# Revit family: HUS-AP-011_EU+APAC_EN
name_source: partatom
category: Casework
units: mm (PartAtom-declared; Revit-internal decimal feet)

## family parameters
Always vertical = Yes
Cut with Voids When Loaded = No
OmniClass Number = 23.40.35.00
OmniClass Title = Casework
Room Calculation Point = Yes
Shared = No
Work Plane-Based = No

## types (640) — shared parameters
Assembly Code = E2010200
Catalogue = https://hushoffice.com
Configurator = https://mikomax.actumwork.pl
Construction Type = Defined construction
Depth = 900 mm  [stored 2.95276 ft]
Equipment - Fixed table = Fixed table : with seat
Equipment - Fixed table with TV mount = Fixed table : with seat + TV holder
Equipment = Movable table = Movable table
Fabric color - seat = ATHLON PLUS Beige
Finish = Defined materials
Handle and hinges = Anodowane aluminium JAL
Height = 2300 mm  [stored 7.54593 ft]
IfcExportAs = IfcFurniture
Manufacturer = Mikomax Smart Office
Region = EU/APAC
Type Image = <None>
URL = https://hushoffice.com
Width = 1245 mm  [stored 4.08465 ft]
zero-valued in all types: Default Elevation

## per-type parameters (varying)
| type | Back glass colour | Counter color | Fabric | Main body | Plug type |
| ABB/001/PRZ/PRZ/EUR/ABB/GPT | Transparent Glass PRZ | White ABB | ATHLON PLUS Blue | White ABB | GPT - Plug type G |
| AGC/001/PRZ/PRZ/EUR/ABB/GPT | Transparent Glass PRZ | White ABB | ATHLON PLUS Blue | Cosmos Grey AGC | GPT - Plug type G |
| ABB/002/PRZ/PRZ/EUR/ABB/GPT | Transparent Glass PRZ | White ABB | ATHLON PLUS Dark grey | White ABB | GPT - Plug type G |
| AGC/002/PRZ/PRZ/EUR/ABB/GPT | Transparent Glass PRZ | White ABB | ATHLON PLUS Dark grey | Cosmos Grey AGC | GPT - Plug type G |
| ABB/003/PRZ/PRZ/EUR/ABB/GPT | Transparent Glass PRZ | White ABB | ATHLON PLUS Light grey | White ABB | GPT - Plug type G |
| AGC/003/PRZ/PRZ/EUR/ABB/GPT | Transparent Glass PRZ | White ABB | ATHLON PLUS Light grey | Cosmos Grey AGC | GPT - Plug type G |
| ABB/004/PRZ/PRZ/EUR/ABB/GPT | Transparent Glass PRZ | White ABB | ATHLON PLUS Light green | White ABB | GPT - Plug type G |
| AGC/004/PRZ/PRZ/EUR/ABB/GPT | Transparent Glass PRZ | White ABB | ATHLON PLUS Light green | Cosmos Grey AGC | GPT - Plug type G |
| ABB/005/PRZ/PRZ/EUR/ABB/GPT | Transparent Glass PRZ | White ABB | ATHLON PLUS Yellow | White ABB | GPT - Plug type G |
| AGC/005/PRZ/PRZ/EUR/ABB/GPT | Transparent Glass PRZ | White ABB | ATHLON PLUS Yellow | Cosmos Grey AGC | GPT - Plug type G |
| ABB/006/PRZ/PRZ/EUR/ABB/GPT | Transparent Glass PRZ | White ABB | ATHLON PLUS Orange | White ABB | GPT - Plug type G |
| AGC/006/PRZ/PRZ/EUR/ABB/GPT | Transparent Glass PRZ | White ABB | ATHLON PLUS Orange | Cosmos Grey AGC | GPT - Plug type G |
| ABB/007/PRZ/PRZ/EUR/ABB/GPT | Transparent Glass PRZ | White ABB | ATHLON PLUS Beige | White ABB | GPT - Plug type G |
| AGC/007/PRZ/PRZ/EUR/ABB/GPT | Transparent Glass PRZ | White ABB | ATHLON PLUS Beige | Cosmos Grey AGC | GPT - Plug type G |
| ABB/008/PRZ/PRZ/EUR/ABB/GPT | Transparent Glass PRZ | White ABB | ATHLON PLUS Red | White ABB | GPT - Plug type G |
| AGC/008/PRZ/PRZ/EUR/ABB/GPT | Transparent Glass PRZ | White ABB | ATHLON PLUS Red | Cosmos Grey AGC | GPT - Plug type G |
| ABB/001/PRZ/MGA/EUR/ABB/GPT | Milk Glass MGA | White ABB | ATHLON PLUS Blue | White ABB | GPT - Plug type G |
| AGC/001/PRZ/MGA/EUR/ABB/GPT | Milk Glass MGA | White ABB | ATHLON PLUS Blue | Cosmos Grey AGC | GPT - Plug type G |
| ABB/002/PRZ/MGA/EUR/ABB/GPT | Milk Glass MGA | White ABB | ATHLON PLUS Dark grey | White ABB | GPT - Plug type G |
| AGC/002/PRZ/MGA/EUR/ABB/GPT | Milk Glass MGA | White ABB | ATHLON PLUS Dark grey | Cosmos Grey AGC | GPT - Plug type G |
| ABB/003/PRZ/MGA/EUR/ABB/GPT | Milk Glass MGA | White ABB | ATHLON PLUS Light grey | White ABB | GPT - Plug type G |
| AGC/003/PRZ/MGA/EUR/ABB/GPT | Milk Glass MGA | White ABB | ATHLON PLUS Light grey | Cosmos Grey AGC | GPT - Plug type G |
| ABB/004/PRZ/MGA/EUR/ABB/GPT | Milk Glass MGA | White ABB | ATHLON PLUS Light green | White ABB | GPT - Plug type G |
| AGC/004/PRZ/MGA/EUR/ABB/GPT | Milk Glass MGA | White ABB | ATHLON PLUS Light green | Cosmos Grey AGC | GPT - Plug type G |
| ABB/005/PRZ/MGA/EUR/ABB/GPT | Milk Glass MGA | White ABB | ATHLON PLUS Yellow | White ABB | GPT - Plug type G |
| AGC/005/PRZ/MGA/EUR/ABB/GPT | Milk Glass MGA | White ABB | ATHLON PLUS Yellow | Cosmos Grey AGC | GPT - Plug type G |
| ABB/006/PRZ/MGA/EUR/ABB/GPT | Milk Glass MGA | White ABB | ATHLON PLUS Orange | White ABB | GPT - Plug type G |
| AGC/006/PRZ/MGA/EUR/ABB/GPT | Milk Glass MGA | White ABB | ATHLON PLUS Orange | Cosmos Grey AGC | GPT - Plug type G |
| ABB/007/PRZ/MGA/EUR/ABB/GPT | Milk Glass MGA | White ABB | ATHLON PLUS Beige | White ABB | GPT - Plug type G |
| AGC/007/PRZ/MGA/EUR/ABB/GPT | Milk Glass MGA | White ABB | ATHLON PLUS Beige | Cosmos Grey AGC | GPT - Plug type G |
| ABB/008/PRZ/MGA/EUR/ABB/GPT | Milk Glass MGA | White ABB | ATHLON PLUS Red | White ABB | GPT - Plug type G |
| AGC/008/PRZ/MGA/EUR/ABB/GPT | Milk Glass MGA | White ABB | ATHLON PLUS Red | Cosmos Grey AGC | GPT - Plug type G |
| ABB/001/PRZ/PRZ/APA/ABB/GPT | Transparent Glass PRZ | White ABB | ATHLON PLUS Blue | White ABB | GPT - Plug type G |
| AGC/001/PRZ/PRZ/APA/ABB/GPT | Transparent Glass PRZ | White ABB | ATHLON PLUS Blue | Cosmos Grey AGC | GPT - Plug type G |
| ABB/002/PRZ/PRZ/APA/ABB/GPT | Transparent Glass PRZ | White ABB | ATHLON PLUS Dark grey | White ABB | GPT - Plug type G |
| AGC/002/PRZ/PRZ/APA/ABB/GPT | Transparent Glass PRZ | White ABB | ATHLON PLUS Dark grey | Cosmos Grey AGC | GPT - Plug type G |
| ABB/003/PRZ/PRZ/APA/ABB/GPT | Transparent Glass PRZ | White ABB | ATHLON PLUS Light grey | White ABB | GPT - Plug type G |
| AGC/003/PRZ/PRZ/APA/ABB/GPT | Transparent Glass PRZ | White ABB | ATHLON PLUS Light grey | Cosmos Grey AGC | GPT - Plug type G |
| ABB/004/PRZ/PRZ/APA/ABB/GPT | Transparent Glass PRZ | White ABB | ATHLON PLUS Light green | White ABB | GPT - Plug type G |
| AGC/004/PRZ/PRZ/APA/ABB/GPT | Transparent Glass PRZ | White ABB | ATHLON PLUS Light green | Cosmos Grey AGC | GPT - Plug type G |
| ABB/005/PRZ/PRZ/APA/ABB/GPT | Transparent Glass PRZ | White ABB | ATHLON PLUS Yellow | White ABB | GPT - Plug type G |
| AGC/005/PRZ/PRZ/APA/ABB/GPT | Transparent Glass PRZ | White ABB | ATHLON PLUS Yellow | Cosmos Grey AGC | GPT - Plug type G |
| ABB/006/PRZ/PRZ/APA/ABB/GPT | Transparent Glass PRZ | White ABB | ATHLON PLUS Orange | White ABB | GPT - Plug type G |
| AGC/006/PRZ/PRZ/APA/ABB/GPT | Transparent Glass PRZ | White ABB | ATHLON PLUS Orange | Cosmos Grey AGC | GPT - Plug type G |
| ABB/007/PRZ/PRZ/APA/ABB/GPT | Transparent Glass PRZ | White ABB | ATHLON PLUS Beige | White ABB | GPT - Plug type G |
| AGC/007/PRZ/PRZ/APA/ABB/GPT | Transparent Glass PRZ | White ABB | ATHLON PLUS Beige | Cosmos Grey AGC | GPT - Plug type G |
| ABB/008/PRZ/PRZ/APA/ABB/GPT | Transparent Glass PRZ | White ABB | ATHLON PLUS Red | White ABB | GPT - Plug type G |
| AGC/008/PRZ/PRZ/APA/ABB/GPT | Transparent Glass PRZ | White ABB | ATHLON PLUS Red | Cosmos Grey AGC | GPT - Plug type G |
| ABB/001/PRZ/MGA/APA/ABB/GPT | Milk Glass MGA | White ABB | ATHLON PLUS Blue | White ABB | GPT - Plug type G |
| AGC/001/PRZ/MGA/APA/ABB/GPT | Milk Glass MGA | White ABB | ATHLON PLUS Blue | Cosmos Grey AGC | GPT - Plug type G |
| ABB/002/PRZ/MGA/APA/ABB/GPT | Milk Glass MGA | White ABB | ATHLON PLUS Dark grey | White ABB | GPT - Plug type G |
| AGC/002/PRZ/MGA/APA/ABB/GPT | Milk Glass MGA | White ABB | ATHLON PLUS Dark grey | Cosmos Grey AGC | GPT - Plug type G |
| ABB/003/PRZ/MGA/APA/ABB/GPT | Milk Glass MGA | White ABB | ATHLON PLUS Light grey | White ABB | GPT - Plug type G |
| AGC/003/PRZ/MGA/APA/ABB/GPT | Milk Glass MGA | White ABB | ATHLON PLUS Light grey | Cosmos Grey AGC | GPT - Plug type G |
| ABB/004/PRZ/MGA/APA/ABB/GPT | Milk Glass MGA | White ABB | ATHLON PLUS Light green | White ABB | GPT - Plug type G |
| AGC/004/PRZ/MGA/APA/ABB/GPT | Milk Glass MGA | White ABB | ATHLON PLUS Light green | Cosmos Grey AGC | GPT - Plug type G |
| ABB/005/PRZ/MGA/APA/ABB/GPT | Milk Glass MGA | White ABB | ATHLON PLUS Yellow | White ABB | GPT - Plug type G |
| AGC/005/PRZ/MGA/APA/ABB/GPT | Milk Glass MGA | White ABB | ATHLON PLUS Yellow | Cosmos Grey AGC | GPT - Plug type G |
| ABB/006/PRZ/MGA/APA/ABB/GPT | Milk Glass MGA | White ABB | ATHLON PLUS Orange | White ABB | GPT - Plug type G |
| AGC/006/PRZ/MGA/APA/ABB/GPT | Milk Glass MGA | White ABB | ATHLON PLUS Orange | Cosmos Grey AGC | GPT - Plug type G |
| ABB/007/PRZ/MGA/APA/ABB/GPT | Milk Glass MGA | White ABB | ATHLON PLUS Beige | White ABB | GPT - Plug type G |
| AGC/007/PRZ/MGA/APA/ABB/GPT | Milk Glass MGA | White ABB | ATHLON PLUS Beige | Cosmos Grey AGC | GPT - Plug type G |
| ABB/008/PRZ/MGA/APA/ABB/GPT | Milk Glass MGA | White ABB | ATHLON PLUS Red | White ABB | GPT - Plug type G |
| AGC/008/PRZ/MGA/APA/ABB/GPT | Milk Glass MGA | White ABB | ATHLON PLUS Red | Cosmos Grey AGC | GPT - Plug type G |
| ABB/001/PRZ/PRZ/EUR/AGA/GPT | Transparent Glass PRZ | Velvet Black AGA | ATHLON PLUS Blue | White ABB | GPT - Plug type G |
| AGC/001/PRZ/PRZ/EUR/AGA/GPT | Transparent Glass PRZ | Velvet Black AGA | ATHLON PLUS Blue | Cosmos Grey AGC | GPT - Plug type G |
| ABB/002/PRZ/PRZ/EUR/AGA/GPT | Transparent Glass PRZ | Velvet Black AGA | ATHLON PLUS Dark grey | White ABB | GPT - Plug type G |
| AGC/002/PRZ/PRZ/EUR/AGA/GPT | Transparent Glass PRZ | Velvet Black AGA | ATHLON PLUS Dark grey | Cosmos Grey AGC | GPT - Plug type G |
| ABB/003/PRZ/PRZ/EUR/AGA/GPT | Transparent Glass PRZ | Velvet Black AGA | ATHLON PLUS Light grey | White ABB | GPT - Plug type G |
| AGC/003/PRZ/PRZ/EUR/AGA/GPT | Transparent Glass PRZ | Velvet Black AGA | ATHLON PLUS Light grey | Cosmos Grey AGC | GPT - Plug type G |
| ABB/004/PRZ/PRZ/EUR/AGA/GPT | Transparent Glass PRZ | Velvet Black AGA | ATHLON PLUS Light green | White ABB | GPT - Plug type G |
| AGC/004/PRZ/PRZ/EUR/AGA/GPT | Transparent Glass PRZ | Velvet Black AGA | ATHLON PLUS Light green | Cosmos Grey AGC | GPT - Plug type G |
| ABB/005/PRZ/PRZ/EUR/AGA/GPT | Transparent Glass PRZ | Velvet Black AGA | ATHLON PLUS Yellow | White ABB | GPT - Plug type G |
| AGC/005/PRZ/PRZ/EUR/AGA/GPT | Transparent Glass PRZ | Velvet Black AGA | ATHLON PLUS Yellow | Cosmos Grey AGC | GPT - Plug type G |
| ABB/006/PRZ/PRZ/EUR/AGA/GPT | Transparent Glass PRZ | Velvet Black AGA | ATHLON PLUS Orange | White ABB | GPT - Plug type G |
| AGC/006/PRZ/PRZ/EUR/AGA/GPT | Transparent Glass PRZ | Velvet Black AGA | ATHLON PLUS Orange | Cosmos Grey AGC | GPT - Plug type G |
| ABB/007/PRZ/PRZ/EUR/AGA/GPT | Transparent Glass PRZ | Velvet Black AGA | ATHLON PLUS Beige | White ABB | GPT - Plug type G |
| AGC/007/PRZ/PRZ/EUR/AGA/GPT | Transparent Glass PRZ | Velvet Black AGA | ATHLON PLUS Beige | Cosmos Grey AGC | GPT - Plug type G |
| ABB/008/PRZ/PRZ/EUR/AGA/GPT | Transparent Glass PRZ | Velvet Black AGA | ATHLON PLUS Red | White ABB | GPT - Plug type G |
| AGC/008/PRZ/PRZ/EUR/AGA/GPT | Transparent Glass PRZ | Velvet Black AGA | ATHLON PLUS Red | Cosmos Grey AGC | GPT - Plug type G |
| ABB/001/PRZ/MGA/EUR/AGA/GPT | Milk Glass MGA | Velvet Black AGA | ATHLON PLUS Blue | White ABB | GPT - Plug type G |
| AGC/001/PRZ/MGA/EUR/AGA/GPT | Milk Glass MGA | Velvet Black AGA | ATHLON PLUS Blue | Cosmos Grey AGC | GPT - Plug type G |
| ABB/002/PRZ/MGA/EUR/AGA/GPT | Milk Glass MGA | Velvet Black AGA | ATHLON PLUS Dark grey | White ABB | GPT - Plug type G |
| AGC/002/PRZ/MGA/EUR/AGA/GPT | Milk Glass MGA | Velvet Black AGA | ATHLON PLUS Dark grey | Cosmos Grey AGC | GPT - Plug type G |
| ABB/003/PRZ/MGA/EUR/AGA/GPT | Milk Glass MGA | Velvet Black AGA | ATHLON PLUS Light grey | White ABB | GPT - Plug type G |
| AGC/003/PRZ/MGA/EUR/AGA/GPT | Milk Glass MGA | Velvet Black AGA | ATHLON PLUS Light grey | Cosmos Grey AGC | GPT - Plug type G |
| ABB/004/PRZ/MGA/EUR/AGA/GPT | Milk Glass MGA | Velvet Black AGA | ATHLON PLUS Light green | White ABB | GPT - Plug type G |
| AGC/004/PRZ/MGA/EUR/AGA/GPT | Milk Glass MGA | Velvet Black AGA | ATHLON PLUS Light green | Cosmos Grey AGC | GPT - Plug type G |
| ABB/005/PRZ/MGA/EUR/AGA/GPT | Milk Glass MGA | Velvet Black AGA | ATHLON PLUS Yellow | White ABB | GPT - Plug type G |
| AGC/005/PRZ/MGA/EUR/AGA/GPT | Milk Glass MGA | Velvet Black AGA | ATHLON PLUS Yellow | Cosmos Grey AGC | GPT - Plug type G |
| ABB/006/PRZ/MGA/EUR/AGA/GPT | Milk Glass MGA | Velvet Black AGA | ATHLON PLUS Orange | White ABB | GPT - Plug type G |
| AGC/006/PRZ/MGA/EUR/AGA/GPT | Milk Glass MGA | Velvet Black AGA | ATHLON PLUS Orange | Cosmos Grey AGC | GPT - Plug type G |
| ABB/007/PRZ/MGA/EUR/AGA/GPT | Milk Glass MGA | Velvet Black AGA | ATHLON PLUS Beige | White ABB | GPT - Plug type G |
| AGC/007/PRZ/MGA/EUR/AGA/GPT | Milk Glass MGA | Velvet Black AGA | ATHLON PLUS Beige | Cosmos Grey AGC | GPT - Plug type G |
| ABB/008/PRZ/MGA/EUR/AGA/GPT | Milk Glass MGA | Velvet Black AGA | ATHLON PLUS Red | White ABB | GPT - Plug type G |
| AGC/008/PRZ/MGA/EUR/AGA/GPT | Milk Glass MGA | Velvet Black AGA | ATHLON PLUS Red | Cosmos Grey AGC | GPT - Plug type G |
| ABB/001/PRZ/PRZ/APA/AGA/GPT | Transparent Glass PRZ | Velvet Black AGA | ATHLON PLUS Blue | White ABB | GPT - Plug type G |
| AGC/001/PRZ/PRZ/APA/AGA/GPT | Transparent Glass PRZ | Velvet Black AGA | ATHLON PLUS Blue | Cosmos Grey AGC | GPT - Plug type G |
| ABB/002/PRZ/PRZ/APA/AGA/GPT | Transparent Glass PRZ | Velvet Black AGA | ATHLON PLUS Dark grey | White ABB | GPT - Plug type G |
| AGC/002/PRZ/PRZ/APA/AGA/GPT | Transparent Glass PRZ | Velvet Black AGA | ATHLON PLUS Dark grey | Cosmos Grey AGC | GPT - Plug type G |
| ABB/003/PRZ/PRZ/APA/AGA/GPT | Transparent Glass PRZ | Velvet Black AGA | ATHLON PLUS Light grey | White ABB | GPT - Plug type G |
| AGC/003/PRZ/PRZ/APA/AGA/GPT | Transparent Glass PRZ | Velvet Black AGA | ATHLON PLUS Light grey | Cosmos Grey AGC | GPT - Plug type G |
| ABB/004/PRZ/PRZ/APA/AGA/GPT | Transparent Glass PRZ | Velvet Black AGA | ATHLON PLUS Light green | White ABB | GPT - Plug type G |
| AGC/004/PRZ/PRZ/APA/AGA/GPT | Transparent Glass PRZ | Velvet Black AGA | ATHLON PLUS Light green | Cosmos Grey AGC | GPT - Plug type G |
| ABB/005/PRZ/PRZ/APA/AGA/GPT | Transparent Glass PRZ | Velvet Black AGA | ATHLON PLUS Yellow | White ABB | GPT - Plug type G |
| AGC/005/PRZ/PRZ/APA/AGA/GPT | Transparent Glass PRZ | Velvet Black AGA | ATHLON PLUS Yellow | Cosmos Grey AGC | GPT - Plug type G |
| ABB/006/PRZ/PRZ/APA/AGA/GPT | Transparent Glass PRZ | Velvet Black AGA | ATHLON PLUS Orange | White ABB | GPT - Plug type G |
| AGC/006/PRZ/PRZ/APA/AGA/GPT | Transparent Glass PRZ | Velvet Black AGA | ATHLON PLUS Orange | Cosmos Grey AGC | GPT - Plug type G |
| ABB/007/PRZ/PRZ/APA/AGA/GPT | Transparent Glass PRZ | Velvet Black AGA | ATHLON PLUS Beige | White ABB | GPT - Plug type G |
| AGC/007/PRZ/PRZ/APA/AGA/GPT | Transparent Glass PRZ | Velvet Black AGA | ATHLON PLUS Beige | Cosmos Grey AGC | GPT - Plug type G |
| ABB/008/PRZ/PRZ/APA/AGA/GPT | Transparent Glass PRZ | Velvet Black AGA | ATHLON PLUS Red | White ABB | GPT - Plug type G |
| AGC/008/PRZ/PRZ/APA/AGA/GPT | Transparent Glass PRZ | Velvet Black AGA | ATHLON PLUS Red | Cosmos Grey AGC | GPT - Plug type G |
| ABB/001/PRZ/MGA/APA/AGA/GPT | Milk Glass MGA | Velvet Black AGA | ATHLON PLUS Blue | White ABB | GPT - Plug type G |
| AGC/001/PRZ/MGA/APA/AGA/GPT | Milk Glass MGA | Velvet Black AGA | ATHLON PLUS Blue | Cosmos Grey AGC | GPT - Plug type G |
| ABB/002/PRZ/MGA/APA/AGA/GPT | Milk Glass MGA | Velvet Black AGA | ATHLON PLUS Dark grey | White ABB | GPT - Plug type G |
| AGC/002/PRZ/MGA/APA/AGA/GPT | Milk Glass MGA | Velvet Black AGA | ATHLON PLUS Dark grey | Cosmos Grey AGC | GPT - Plug type G |
| ABB/003/PRZ/MGA/APA/AGA/GPT | Milk Glass MGA | Velvet Black AGA | ATHLON PLUS Light grey | White ABB | GPT - Plug type G |
| AGC/003/PRZ/MGA/APA/AGA/GPT | Milk Glass MGA | Velvet Black AGA | ATHLON PLUS Light grey | Cosmos Grey AGC | GPT - Plug type G |
| ABB/004/PRZ/MGA/APA/AGA/GPT | Milk Glass MGA | Velvet Black AGA | ATHLON PLUS Light green | White ABB | GPT - Plug type G |
| AGC/004/PRZ/MGA/APA/AGA/GPT | Milk Glass MGA | Velvet Black AGA | ATHLON PLUS Light green | Cosmos Grey AGC | GPT - Plug type G |
| ABB/005/PRZ/MGA/APA/AGA/GPT | Milk Glass MGA | Velvet Black AGA | ATHLON PLUS Yellow | White ABB | GPT - Plug type G |
| AGC/005/PRZ/MGA/APA/AGA/GPT | Milk Glass MGA | Velvet Black AGA | ATHLON PLUS Yellow | Cosmos Grey AGC | GPT - Plug type G |
| ABB/006/PRZ/MGA/APA/AGA/GPT | Milk Glass MGA | Velvet Black AGA | ATHLON PLUS Orange | White ABB | GPT - Plug type G |
| AGC/006/PRZ/MGA/APA/AGA/GPT | Milk Glass MGA | Velvet Black AGA | ATHLON PLUS Orange | Cosmos Grey AGC | GPT - Plug type G |
| ABB/007/PRZ/MGA/APA/AGA/GPT | Milk Glass MGA | Velvet Black AGA | ATHLON PLUS Beige | White ABB | GPT - Plug type G |
| AGC/007/PRZ/MGA/APA/AGA/GPT | Milk Glass MGA | Velvet Black AGA | ATHLON PLUS Beige | Cosmos Grey AGC | GPT - Plug type G |
| ABB/008/PRZ/MGA/APA/AGA/GPT | Milk Glass MGA | Velvet Black AGA | ATHLON PLUS Red | White ABB | GPT - Plug type G |
| AGC/008/PRZ/MGA/APA/AGA/GPT | Milk Glass MGA | Velvet Black AGA | ATHLON PLUS Red | Cosmos Grey AGC | GPT - Plug type G |
| ABB/001/PRZ/PRZ/EUR/ABB/FPT | Transparent Glass PRZ | White ABB | ATHLON PLUS Blue | White ABB | FPT - Plug type F |
| AGC/001/PRZ/PRZ/EUR/ABB/FPT | Transparent Glass PRZ | White ABB | ATHLON PLUS Blue | Cosmos Grey AGC | FPT - Plug type F |
| ABB/002/PRZ/PRZ/EUR/ABB/FPT | Transparent Glass PRZ | White ABB | ATHLON PLUS Dark grey | White ABB | FPT - Plug type F |
| AGC/002/PRZ/PRZ/EUR/ABB/FPT | Transparent Glass PRZ | White ABB | ATHLON PLUS Dark grey | Cosmos Grey AGC | FPT - Plug type F |
| ABB/003/PRZ/PRZ/EUR/ABB/FPT | Transparent Glass PRZ | White ABB | ATHLON PLUS Light grey | White ABB | FPT - Plug type F |
| AGC/003/PRZ/PRZ/EUR/ABB/FPT | Transparent Glass PRZ | White ABB | ATHLON PLUS Light grey | Cosmos Grey AGC | FPT - Plug type F |
| ABB/004/PRZ/PRZ/EUR/ABB/FPT | Transparent Glass PRZ | White ABB | ATHLON PLUS Light green | White ABB | FPT - Plug type F |
| AGC/004/PRZ/PRZ/EUR/ABB/FPT | Transparent Glass PRZ | White ABB | ATHLON PLUS Light green | Cosmos Grey AGC | FPT - Plug type F |
| ABB/005/PRZ/PRZ/EUR/ABB/FPT | Transparent Glass PRZ | White ABB | ATHLON PLUS Yellow | White ABB | FPT - Plug type F |
| AGC/005/PRZ/PRZ/EUR/ABB/FPT | Transparent Glass PRZ | White ABB | ATHLON PLUS Yellow | Cosmos Grey AGC | FPT - Plug type F |
| ABB/006/PRZ/PRZ/EUR/ABB/FPT | Transparent Glass PRZ | White ABB | ATHLON PLUS Orange | White ABB | FPT - Plug type F |
| AGC/006/PRZ/PRZ/EUR/ABB/FPT | Transparent Glass PRZ | White ABB | ATHLON PLUS Orange | Cosmos Grey AGC | FPT - Plug type F |
| ABB/007/PRZ/PRZ/EUR/ABB/FPT | Transparent Glass PRZ | White ABB | ATHLON PLUS Beige | White ABB | FPT - Plug type F |
| AGC/007/PRZ/PRZ/EUR/ABB/FPT | Transparent Glass PRZ | White ABB | ATHLON PLUS Beige | Cosmos Grey AGC | FPT - Plug type F |
| ABB/008/PRZ/PRZ/EUR/ABB/FPT | Transparent Glass PRZ | White ABB | ATHLON PLUS Red | White ABB | FPT - Plug type F |
| AGC/008/PRZ/PRZ/EUR/ABB/FPT | Transparent Glass PRZ | White ABB | ATHLON PLUS Red | Cosmos Grey AGC | FPT - Plug type F |
| ABB/001/PRZ/MGA/EUR/ABB/FPT | Milk Glass MGA | White ABB | ATHLON PLUS Blue | White ABB | FPT - Plug type F |
| AGC/001/PRZ/MGA/EUR/ABB/FPT | Milk Glass MGA | White ABB | ATHLON PLUS Blue | Cosmos Grey AGC | FPT - Plug type F |
| ABB/002/PRZ/MGA/EUR/ABB/FPT | Milk Glass MGA | White ABB | ATHLON PLUS Dark grey | White ABB | FPT - Plug type F |
| AGC/002/PRZ/MGA/EUR/ABB/FPT | Milk Glass MGA | White ABB | ATHLON PLUS Dark grey | Cosmos Grey AGC | FPT - Plug type F |
| ABB/003/PRZ/MGA/EUR/ABB/FPT | Milk Glass MGA | White ABB | ATHLON PLUS Light grey | White ABB | FPT - Plug type F |
| AGC/003/PRZ/MGA/EUR/ABB/FPT | Milk Glass MGA | White ABB | ATHLON PLUS Light grey | Cosmos Grey AGC | FPT - Plug type F |
| ABB/004/PRZ/MGA/EUR/ABB/FPT | Milk Glass MGA | White ABB | ATHLON PLUS Light green | White ABB | FPT - Plug type F |
| AGC/004/PRZ/MGA/EUR/ABB/FPT | Milk Glass MGA | White ABB | ATHLON PLUS Light green | Cosmos Grey AGC | FPT - Plug type F |
| ABB/005/PRZ/MGA/EUR/ABB/FPT | Milk Glass MGA | White ABB | ATHLON PLUS Yellow | White ABB | FPT - Plug type F |
| AGC/005/PRZ/MGA/EUR/ABB/FPT | Milk Glass MGA | White ABB | ATHLON PLUS Yellow | Cosmos Grey AGC | FPT - Plug type F |
| ABB/006/PRZ/MGA/EUR/ABB/FPT | Milk Glass MGA | White ABB | ATHLON PLUS Orange | White ABB | FPT - Plug type F |
| AGC/006/PRZ/MGA/EUR/ABB/FPT | Milk Glass MGA | White ABB | ATHLON PLUS Orange | Cosmos Grey AGC | FPT - Plug type F |
| ABB/007/PRZ/MGA/EUR/ABB/FPT | Milk Glass MGA | White ABB | ATHLON PLUS Beige | White ABB | FPT - Plug type F |
| AGC/007/PRZ/MGA/EUR/ABB/FPT | Milk Glass MGA | White ABB | ATHLON PLUS Beige | Cosmos Grey AGC | FPT - Plug type F |
| ABB/008/PRZ/MGA/EUR/ABB/FPT | Milk Glass MGA | White ABB | ATHLON PLUS Red | White ABB | FPT - Plug type F |
| AGC/008/PRZ/MGA/EUR/ABB/FPT | Milk Glass MGA | White ABB | ATHLON PLUS Red | Cosmos Grey AGC | FPT - Plug type F |
| ABB/001/PRZ/PRZ/APA/ABB/FPT | Transparent Glass PRZ | White ABB | ATHLON PLUS Blue | White ABB | FPT - Plug type F |
| AGC/001/PRZ/PRZ/APA/ABB/FPT | Transparent Glass PRZ | White ABB | ATHLON PLUS Blue | Cosmos Grey AGC | FPT - Plug type F |
| ABB/002/PRZ/PRZ/APA/ABB/FPT | Transparent Glass PRZ | White ABB | ATHLON PLUS Dark grey | White ABB | FPT - Plug type F |
| AGC/002/PRZ/PRZ/APA/ABB/FPT | Transparent Glass PRZ | White ABB | ATHLON PLUS Dark grey | Cosmos Grey AGC | FPT - Plug type F |
| ABB/003/PRZ/PRZ/APA/ABB/FPT | Transparent Glass PRZ | White ABB | ATHLON PLUS Light grey | White ABB | FPT - Plug type F |
| AGC/003/PRZ/PRZ/APA/ABB/FPT | Transparent Glass PRZ | White ABB | ATHLON PLUS Light grey | Cosmos Grey AGC | FPT - Plug type F |
| ABB/004/PRZ/PRZ/APA/ABB/FPT | Transparent Glass PRZ | White ABB | ATHLON PLUS Light green | White ABB | FPT - Plug type F |
| AGC/004/PRZ/PRZ/APA/ABB/FPT | Transparent Glass PRZ | White ABB | ATHLON PLUS Light green | Cosmos Grey AGC | FPT - Plug type F |
| ABB/005/PRZ/PRZ/APA/ABB/FPT | Transparent Glass PRZ | White ABB | ATHLON PLUS Yellow | White ABB | FPT - Plug type F |
| AGC/005/PRZ/PRZ/APA/ABB/FPT | Transparent Glass PRZ | White ABB | ATHLON PLUS Yellow | Cosmos Grey AGC | FPT - Plug type F |
| ABB/006/PRZ/PRZ/APA/ABB/FPT | Transparent Glass PRZ | White ABB | ATHLON PLUS Orange | White ABB | FPT - Plug type F |
| AGC/006/PRZ/PRZ/APA/ABB/FPT | Transparent Glass PRZ | White ABB | ATHLON PLUS Orange | Cosmos Grey AGC | FPT - Plug type F |
| ABB/007/PRZ/PRZ/APA/ABB/FPT | Transparent Glass PRZ | White ABB | ATHLON PLUS Beige | White ABB | FPT - Plug type F |
| AGC/007/PRZ/PRZ/APA/ABB/FPT | Transparent Glass PRZ | White ABB | ATHLON PLUS Beige | Cosmos Grey AGC | FPT - Plug type F |
| ABB/008/PRZ/PRZ/APA/ABB/FPT | Transparent Glass PRZ | White ABB | ATHLON PLUS Red | White ABB | FPT - Plug type F |
| AGC/008/PRZ/PRZ/APA/ABB/FPT | Transparent Glass PRZ | White ABB | ATHLON PLUS Red | Cosmos Grey AGC | FPT - Plug type F |
| ABB/001/PRZ/MGA/APA/ABB/FPT | Milk Glass MGA | White ABB | ATHLON PLUS Blue | White ABB | FPT - Plug type F |
| AGC/001/PRZ/MGA/APA/ABB/FPT | Milk Glass MGA | White ABB | ATHLON PLUS Blue | Cosmos Grey AGC | FPT - Plug type F |
| ABB/002/PRZ/MGA/APA/ABB/FPT | Milk Glass MGA | White ABB | ATHLON PLUS Dark grey | White ABB | FPT - Plug type F |
| AGC/002/PRZ/MGA/APA/ABB/FPT | Milk Glass MGA | White ABB | ATHLON PLUS Dark grey | Cosmos Grey AGC | FPT - Plug type F |
| ABB/003/PRZ/MGA/APA/ABB/FPT | Milk Glass MGA | White ABB | ATHLON PLUS Light grey | White ABB | FPT - Plug type F |
| AGC/003/PRZ/MGA/APA/ABB/FPT | Milk Glass MGA | White ABB | ATHLON PLUS Light grey | Cosmos Grey AGC | FPT - Plug type F |
| ABB/004/PRZ/MGA/APA/ABB/FPT | Milk Glass MGA | White ABB | ATHLON PLUS Light green | White ABB | FPT - Plug type F |
| AGC/004/PRZ/MGA/APA/ABB/FPT | Milk Glass MGA | White ABB | ATHLON PLUS Light green | Cosmos Grey AGC | FPT - Plug type F |
| ABB/005/PRZ/MGA/APA/ABB/FPT | Milk Glass MGA | White ABB | ATHLON PLUS Yellow | White ABB | FPT - Plug type F |
| AGC/005/PRZ/MGA/APA/ABB/FPT | Milk Glass MGA | White ABB | ATHLON PLUS Yellow | Cosmos Grey AGC | FPT - Plug type F |
| ABB/006/PRZ/MGA/APA/ABB/FPT | Milk Glass MGA | White ABB | ATHLON PLUS Orange | White ABB | FPT - Plug type F |
| AGC/006/PRZ/MGA/APA/ABB/FPT | Milk Glass MGA | White ABB | ATHLON PLUS Orange | Cosmos Grey AGC | FPT - Plug type F |
| ABB/007/PRZ/MGA/APA/ABB/FPT | Milk Glass MGA | White ABB | ATHLON PLUS Beige | White ABB | FPT - Plug type F |
| AGC/007/PRZ/MGA/APA/ABB/FPT | Milk Glass MGA | White ABB | ATHLON PLUS Beige | Cosmos Grey AGC | FPT - Plug type F |
| ABB/008/PRZ/MGA/APA/ABB/FPT | Milk Glass MGA | White ABB | ATHLON PLUS Red | White ABB | FPT - Plug type F |
| AGC/008/PRZ/MGA/APA/ABB/FPT | Milk Glass MGA | White ABB | ATHLON PLUS Red | Cosmos Grey AGC | FPT - Plug type F |
| ABB/001/PRZ/PRZ/EUR/AGA/FPT | Transparent Glass PRZ | Velvet Black AGA | ATHLON PLUS Blue | White ABB | FPT - Plug type F |
| AGC/001/PRZ/PRZ/EUR/AGA/FPT | Transparent Glass PRZ | Velvet Black AGA | ATHLON PLUS Blue | Cosmos Grey AGC | FPT - Plug type F |
| ABB/002/PRZ/PRZ/EUR/AGA/FPT | Transparent Glass PRZ | Velvet Black AGA | ATHLON PLUS Dark grey | White ABB | FPT - Plug type F |
| AGC/002/PRZ/PRZ/EUR/AGA/FPT | Transparent Glass PRZ | Velvet Black AGA | ATHLON PLUS Dark grey | Cosmos Grey AGC | FPT - Plug type F |
| ABB/003/PRZ/PRZ/EUR/AGA/FPT | Transparent Glass PRZ | Velvet Black AGA | ATHLON PLUS Light grey | White ABB | FPT - Plug type F |
| AGC/003/PRZ/PRZ/EUR/AGA/FPT | Transparent Glass PRZ | Velvet Black AGA | ATHLON PLUS Light grey | Cosmos Grey AGC | FPT - Plug type F |
| ABB/004/PRZ/PRZ/EUR/AGA/FPT | Transparent Glass PRZ | Velvet Black AGA | ATHLON PLUS Light green | White ABB | FPT - Plug type F |
| AGC/004/PRZ/PRZ/EUR/AGA/FPT | Transparent Glass PRZ | Velvet Black AGA | ATHLON PLUS Light green | Cosmos Grey AGC | FPT - Plug type F |
| ABB/005/PRZ/PRZ/EUR/AGA/FPT | Transparent Glass PRZ | Velvet Black AGA | ATHLON PLUS Yellow | White ABB | FPT - Plug type F |
| AGC/005/PRZ/PRZ/EUR/AGA/FPT | Transparent Glass PRZ | Velvet Black AGA | ATHLON PLUS Yellow | Cosmos Grey AGC | FPT - Plug type F |
| ABB/006/PRZ/PRZ/EUR/AGA/FPT | Transparent Glass PRZ | Velvet Black AGA | ATHLON PLUS Orange | White ABB | FPT - Plug type F |
| AGC/006/PRZ/PRZ/EUR/AGA/FPT | Transparent Glass PRZ | Velvet Black AGA | ATHLON PLUS Orange | Cosmos Grey AGC | FPT - Plug type F |
| ABB/007/PRZ/PRZ/EUR/AGA/FPT | Transparent Glass PRZ | Velvet Black AGA | ATHLON PLUS Beige | White ABB | FPT - Plug type F |
| AGC/007/PRZ/PRZ/EUR/AGA/FPT | Transparent Glass PRZ | Velvet Black AGA | ATHLON PLUS Beige | Cosmos Grey AGC | FPT - Plug type F |
| ABB/008/PRZ/PRZ/EUR/AGA/FPT | Transparent Glass PRZ | Velvet Black AGA | ATHLON PLUS Red | White ABB | FPT - Plug type F |
| AGC/008/PRZ/PRZ/EUR/AGA/FPT | Transparent Glass PRZ | Velvet Black AGA | ATHLON PLUS Red | Cosmos Grey AGC | FPT - Plug type F |
| ABB/001/PRZ/MGA/EUR/AGA/FPT | Milk Glass MGA | Velvet Black AGA | ATHLON PLUS Blue | White ABB | FPT - Plug type F |
| AGC/001/PRZ/MGA/EUR/AGA/FPT | Milk Glass MGA | Velvet Black AGA | ATHLON PLUS Blue | Cosmos Grey AGC | FPT - Plug type F |
| ABB/002/PRZ/MGA/EUR/AGA/FPT | Milk Glass MGA | Velvet Black AGA | ATHLON PLUS Dark grey | White ABB | FPT - Plug type F |
| AGC/002/PRZ/MGA/EUR/AGA/FPT | Milk Glass MGA | Velvet Black AGA | ATHLON PLUS Dark grey | Cosmos Grey AGC | FPT - Plug type F |
| ABB/003/PRZ/MGA/EUR/AGA/FPT | Milk Glass MGA | Velvet Black AGA | ATHLON PLUS Light grey | White ABB | FPT - Plug type F |
| AGC/003/PRZ/MGA/EUR/AGA/FPT | Milk Glass MGA | Velvet Black AGA | ATHLON PLUS Light grey | Cosmos Grey AGC | FPT - Plug type F |
| ABB/004/PRZ/MGA/EUR/AGA/FPT | Milk Glass MGA | Velvet Black AGA | ATHLON PLUS Light green | White ABB | FPT - Plug type F |
| AGC/004/PRZ/MGA/EUR/AGA/FPT | Milk Glass MGA | Velvet Black AGA | ATHLON PLUS Light green | Cosmos Grey AGC | FPT - Plug type F |
| ABB/005/PRZ/MGA/EUR/AGA/FPT | Milk Glass MGA | Velvet Black AGA | ATHLON PLUS Yellow | White ABB | FPT - Plug type F |
| AGC/005/PRZ/MGA/EUR/AGA/FPT | Milk Glass MGA | Velvet Black AGA | ATHLON PLUS Yellow | Cosmos Grey AGC | FPT - Plug type F |
| ABB/006/PRZ/MGA/EUR/AGA/FPT | Milk Glass MGA | Velvet Black AGA | ATHLON PLUS Orange | White ABB | FPT - Plug type F |
| AGC/006/PRZ/MGA/EUR/AGA/FPT | Milk Glass MGA | Velvet Black AGA | ATHLON PLUS Orange | Cosmos Grey AGC | FPT - Plug type F |
| ABB/007/PRZ/MGA/EUR/AGA/FPT | Milk Glass MGA | Velvet Black AGA | ATHLON PLUS Beige | White ABB | FPT - Plug type F |
| AGC/007/PRZ/MGA/EUR/AGA/FPT | Milk Glass MGA | Velvet Black AGA | ATHLON PLUS Beige | Cosmos Grey AGC | FPT - Plug type F |
| ABB/008/PRZ/MGA/EUR/AGA/FPT | Milk Glass MGA | Velvet Black AGA | ATHLON PLUS Red | White ABB | FPT - Plug type F |
| AGC/008/PRZ/MGA/EUR/AGA/FPT | Milk Glass MGA | Velvet Black AGA | ATHLON PLUS Red | Cosmos Grey AGC | FPT - Plug type F |
| ABB/001/PRZ/PRZ/APA/AGA/FPT | Transparent Glass PRZ | Velvet Black AGA | ATHLON PLUS Blue | White ABB | FPT - Plug type F |
| AGC/001/PRZ/PRZ/APA/AGA/FPT | Transparent Glass PRZ | Velvet Black AGA | ATHLON PLUS Blue | Cosmos Grey AGC | FPT - Plug type F |
| ABB/002/PRZ/PRZ/APA/AGA/FPT | Transparent Glass PRZ | Velvet Black AGA | ATHLON PLUS Dark grey | White ABB | FPT - Plug type F |
| AGC/002/PRZ/PRZ/APA/AGA/FPT | Transparent Glass PRZ | Velvet Black AGA | ATHLON PLUS Dark grey | Cosmos Grey AGC | FPT - Plug type F |
| ABB/003/PRZ/PRZ/APA/AGA/FPT | Transparent Glass PRZ | Velvet Black AGA | ATHLON PLUS Light grey | White ABB | FPT - Plug type F |
| AGC/003/PRZ/PRZ/APA/AGA/FPT | Transparent Glass PRZ | Velvet Black AGA | ATHLON PLUS Light grey | Cosmos Grey AGC | FPT - Plug type F |
| ABB/004/PRZ/PRZ/APA/AGA/FPT | Transparent Glass PRZ | Velvet Black AGA | ATHLON PLUS Light green | White ABB | FPT - Plug type F |
| AGC/004/PRZ/PRZ/APA/AGA/FPT | Transparent Glass PRZ | Velvet Black AGA | ATHLON PLUS Light green | Cosmos Grey AGC | FPT - Plug type F |
| ABB/005/PRZ/PRZ/APA/AGA/FPT | Transparent Glass PRZ | Velvet Black AGA | ATHLON PLUS Yellow | White ABB | FPT - Plug type F |
| AGC/005/PRZ/PRZ/APA/AGA/FPT | Transparent Glass PRZ | Velvet Black AGA | ATHLON PLUS Yellow | Cosmos Grey AGC | FPT - Plug type F |
| ABB/006/PRZ/PRZ/APA/AGA/FPT | Transparent Glass PRZ | Velvet Black AGA | ATHLON PLUS Orange | White ABB | FPT - Plug type F |
| AGC/006/PRZ/PRZ/APA/AGA/FPT | Transparent Glass PRZ | Velvet Black AGA | ATHLON PLUS Orange | Cosmos Grey AGC | FPT - Plug type F |
| ABB/007/PRZ/PRZ/APA/AGA/FPT | Transparent Glass PRZ | Velvet Black AGA | ATHLON PLUS Beige | White ABB | FPT - Plug type F |
| AGC/007/PRZ/PRZ/APA/AGA/FPT | Transparent Glass PRZ | Velvet Black AGA | ATHLON PLUS Beige | Cosmos Grey AGC | FPT - Plug type F |
| ABB/008/PRZ/PRZ/APA/AGA/FPT | Transparent Glass PRZ | Velvet Black AGA | ATHLON PLUS Red | White ABB | FPT - Plug type F |
| AGC/008/PRZ/PRZ/APA/AGA/FPT | Transparent Glass PRZ | Velvet Black AGA | ATHLON PLUS Red | Cosmos Grey AGC | FPT - Plug type F |
| ABB/001/PRZ/MGA/APA/AGA/FPT | Milk Glass MGA | Velvet Black AGA | ATHLON PLUS Blue | White ABB | FPT - Plug type F |
| AGC/001/PRZ/MGA/APA/AGA/FPT | Milk Glass MGA | Velvet Black AGA | ATHLON PLUS Blue | Cosmos Grey AGC | FPT - Plug type F |
| ABB/002/PRZ/MGA/APA/AGA/FPT | Milk Glass MGA | Velvet Black AGA | ATHLON PLUS Dark grey | White ABB | FPT - Plug type F |
| AGC/002/PRZ/MGA/APA/AGA/FPT | Milk Glass MGA | Velvet Black AGA | ATHLON PLUS Dark grey | Cosmos Grey AGC | FPT - Plug type F |
| ABB/003/PRZ/MGA/APA/AGA/FPT | Milk Glass MGA | Velvet Black AGA | ATHLON PLUS Light grey | White ABB | FPT - Plug type F |
| AGC/003/PRZ/MGA/APA/AGA/FPT | Milk Glass MGA | Velvet Black AGA | ATHLON PLUS Light grey | Cosmos Grey AGC | FPT - Plug type F |
| ABB/004/PRZ/MGA/APA/AGA/FPT | Milk Glass MGA | Velvet Black AGA | ATHLON PLUS Light green | White ABB | FPT - Plug type F |
| AGC/004/PRZ/MGA/APA/AGA/FPT | Milk Glass MGA | Velvet Black AGA | ATHLON PLUS Light green | Cosmos Grey AGC | FPT - Plug type F |
| ABB/005/PRZ/MGA/APA/AGA/FPT | Milk Glass MGA | Velvet Black AGA | ATHLON PLUS Yellow | White ABB | FPT - Plug type F |
| AGC/005/PRZ/MGA/APA/AGA/FPT | Milk Glass MGA | Velvet Black AGA | ATHLON PLUS Yellow | Cosmos Grey AGC | FPT - Plug type F |
| ABB/006/PRZ/MGA/APA/AGA/FPT | Milk Glass MGA | Velvet Black AGA | ATHLON PLUS Orange | White ABB | FPT - Plug type F |
| AGC/006/PRZ/MGA/APA/AGA/FPT | Milk Glass MGA | Velvet Black AGA | ATHLON PLUS Orange | Cosmos Grey AGC | FPT - Plug type F |
| ABB/007/PRZ/MGA/APA/AGA/FPT | Milk Glass MGA | Velvet Black AGA | ATHLON PLUS Beige | White ABB | FPT - Plug type F |
| AGC/007/PRZ/MGA/APA/AGA/FPT | Milk Glass MGA | Velvet Black AGA | ATHLON PLUS Beige | Cosmos Grey AGC | FPT - Plug type F |
| ABB/008/PRZ/MGA/APA/AGA/FPT | Milk Glass MGA | Velvet Black AGA | ATHLON PLUS Red | White ABB | FPT - Plug type F |
| AGC/008/PRZ/MGA/APA/AGA/FPT | Milk Glass MGA | Velvet Black AGA | ATHLON PLUS Red | Cosmos Grey AGC | FPT - Plug type F |
| ABB/001/PRZ/PRZ/EUR/ABB/EPT | Transparent Glass PRZ | White ABB | ATHLON PLUS Blue | White ABB | EPT - Plug type E |
| AGC/001/PRZ/PRZ/EUR/ABB/EPT | Transparent Glass PRZ | White ABB | ATHLON PLUS Blue | Cosmos Grey AGC | EPT - Plug type E |
| ABB/002/PRZ/PRZ/EUR/ABB/EPT | Transparent Glass PRZ | White ABB | ATHLON PLUS Dark grey | White ABB | EPT - Plug type E |
| AGC/002/PRZ/PRZ/EUR/ABB/EPT | Transparent Glass PRZ | White ABB | ATHLON PLUS Dark grey | Cosmos Grey AGC | EPT - Plug type E |
| ABB/003/PRZ/PRZ/EUR/ABB/EPT | Transparent Glass PRZ | White ABB | ATHLON PLUS Light grey | White ABB | EPT - Plug type E |
| AGC/003/PRZ/PRZ/EUR/ABB/EPT | Transparent Glass PRZ | White ABB | ATHLON PLUS Light grey | Cosmos Grey AGC | EPT - Plug type E |
| ABB/004/PRZ/PRZ/EUR/ABB/EPT | Transparent Glass PRZ | White ABB | ATHLON PLUS Light green | White ABB | EPT - Plug type E |
| AGC/004/PRZ/PRZ/EUR/ABB/EPT | Transparent Glass PRZ | White ABB | ATHLON PLUS Light green | Cosmos Grey AGC | EPT - Plug type E |
| ABB/005/PRZ/PRZ/EUR/ABB/EPT | Transparent Glass PRZ | White ABB | ATHLON PLUS Yellow | White ABB | EPT - Plug type E |
| AGC/005/PRZ/PRZ/EUR/ABB/EPT | Transparent Glass PRZ | White ABB | ATHLON PLUS Yellow | Cosmos Grey AGC | EPT - Plug type E |
| ABB/006/PRZ/PRZ/EUR/ABB/EPT | Transparent Glass PRZ | White ABB | ATHLON PLUS Orange | White ABB | EPT - Plug type E |
| AGC/006/PRZ/PRZ/EUR/ABB/EPT | Transparent Glass PRZ | White ABB | ATHLON PLUS Orange | Cosmos Grey AGC | EPT - Plug type E |
| ABB/007/PRZ/PRZ/EUR/ABB/EPT | Transparent Glass PRZ | White ABB | ATHLON PLUS Beige | White ABB | EPT - Plug type E |
| AGC/007/PRZ/PRZ/EUR/ABB/EPT | Transparent Glass PRZ | White ABB | ATHLON PLUS Beige | Cosmos Grey AGC | EPT - Plug type E |
| ABB/008/PRZ/PRZ/EUR/ABB/EPT | Transparent Glass PRZ | White ABB | ATHLON PLUS Red | White ABB | EPT - Plug type E |
| AGC/008/PRZ/PRZ/EUR/ABB/EPT | Transparent Glass PRZ | White ABB | ATHLON PLUS Red | Cosmos Grey AGC | EPT - Plug type E |
| ABB/001/PRZ/MGA/EUR/ABB/EPT | Milk Glass MGA | White ABB | ATHLON PLUS Blue | White ABB | EPT - Plug type E |
| AGC/001/PRZ/MGA/EUR/ABB/EPT | Milk Glass MGA | White ABB | ATHLON PLUS Blue | Cosmos Grey AGC | EPT - Plug type E |
| ABB/002/PRZ/MGA/EUR/ABB/EPT | Milk Glass MGA | White ABB | ATHLON PLUS Dark grey | White ABB | EPT - Plug type E |
| AGC/002/PRZ/MGA/EUR/ABB/EPT | Milk Glass MGA | White ABB | ATHLON PLUS Dark grey | Cosmos Grey AGC | EPT - Plug type E |
| ABB/003/PRZ/MGA/EUR/ABB/EPT | Milk Glass MGA | White ABB | ATHLON PLUS Light grey | White ABB | EPT - Plug type E |
| AGC/003/PRZ/MGA/EUR/ABB/EPT | Milk Glass MGA | White ABB | ATHLON PLUS Light grey | Cosmos Grey AGC | EPT - Plug type E |
| ABB/004/PRZ/MGA/EUR/ABB/EPT | Milk Glass MGA | White ABB | ATHLON PLUS Light green | White ABB | EPT - Plug type E |
| AGC/004/PRZ/MGA/EUR/ABB/EPT | Milk Glass MGA | White ABB | ATHLON PLUS Light green | Cosmos Grey AGC | EPT - Plug type E |
| ABB/005/PRZ/MGA/EUR/ABB/EPT | Milk Glass MGA | White ABB | ATHLON PLUS Yellow | White ABB | EPT - Plug type E |
| AGC/005/PRZ/MGA/EUR/ABB/EPT | Milk Glass MGA | White ABB | ATHLON PLUS Yellow | Cosmos Grey AGC | EPT - Plug type E |
| ABB/006/PRZ/MGA/EUR/ABB/EPT | Milk Glass MGA | White ABB | ATHLON PLUS Orange | White ABB | EPT - Plug type E |
| AGC/006/PRZ/MGA/EUR/ABB/EPT | Milk Glass MGA | White ABB | ATHLON PLUS Orange | Cosmos Grey AGC | EPT - Plug type E |
| ABB/007/PRZ/MGA/EUR/ABB/EPT | Milk Glass MGA | White ABB | ATHLON PLUS Beige | White ABB | EPT - Plug type E |
| AGC/007/PRZ/MGA/EUR/ABB/EPT | Milk Glass MGA | White ABB | ATHLON PLUS Beige | Cosmos Grey AGC | EPT - Plug type E |
| ABB/008/PRZ/MGA/EUR/ABB/EPT | Milk Glass MGA | White ABB | ATHLON PLUS Red | White ABB | EPT - Plug type E |
| AGC/008/PRZ/MGA/EUR/ABB/EPT | Milk Glass MGA | White ABB | ATHLON PLUS Red | Cosmos Grey AGC | EPT - Plug type E |
| ABB/001/PRZ/PRZ/APA/ABB/EPT | Transparent Glass PRZ | White ABB | ATHLON PLUS Blue | White ABB | EPT - Plug type E |
| AGC/001/PRZ/PRZ/APA/ABB/EPT | Transparent Glass PRZ | White ABB | ATHLON PLUS Blue | Cosmos Grey AGC | EPT - Plug type E |
| ABB/002/PRZ/PRZ/APA/ABB/EPT | Transparent Glass PRZ | White ABB | ATHLON PLUS Dark grey | White ABB | EPT - Plug type E |
| AGC/002/PRZ/PRZ/APA/ABB/EPT | Transparent Glass PRZ | White ABB | ATHLON PLUS Dark grey | Cosmos Grey AGC | EPT - Plug type E |
| ABB/003/PRZ/PRZ/APA/ABB/EPT | Transparent Glass PRZ | White ABB | ATHLON PLUS Light grey | White ABB | EPT - Plug type E |
| AGC/003/PRZ/PRZ/APA/ABB/EPT | Transparent Glass PRZ | White ABB | ATHLON PLUS Light grey | Cosmos Grey AGC | EPT - Plug type E |
| ABB/004/PRZ/PRZ/APA/ABB/EPT | Transparent Glass PRZ | White ABB | ATHLON PLUS Light green | White ABB | EPT - Plug type E |
| AGC/004/PRZ/PRZ/APA/ABB/EPT | Transparent Glass PRZ | White ABB | ATHLON PLUS Light green | Cosmos Grey AGC | EPT - Plug type E |
| ABB/005/PRZ/PRZ/APA/ABB/EPT | Transparent Glass PRZ | White ABB | ATHLON PLUS Yellow | White ABB | EPT - Plug type E |
| AGC/005/PRZ/PRZ/APA/ABB/EPT | Transparent Glass PRZ | White ABB | ATHLON PLUS Yellow | Cosmos Grey AGC | EPT - Plug type E |
| ABB/006/PRZ/PRZ/APA/ABB/EPT | Transparent Glass PRZ | White ABB | ATHLON PLUS Orange | White ABB | EPT - Plug type E |
| AGC/006/PRZ/PRZ/APA/ABB/EPT | Transparent Glass PRZ | White ABB | ATHLON PLUS Orange | Cosmos Grey AGC | EPT - Plug type E |
| ABB/007/PRZ/PRZ/APA/ABB/EPT | Transparent Glass PRZ | White ABB | ATHLON PLUS Beige | White ABB | EPT - Plug type E |
| AGC/007/PRZ/PRZ/APA/ABB/EPT | Transparent Glass PRZ | White ABB | ATHLON PLUS Beige | Cosmos Grey AGC | EPT - Plug type E |
| ABB/008/PRZ/PRZ/APA/ABB/EPT | Transparent Glass PRZ | White ABB | ATHLON PLUS Red | White ABB | EPT - Plug type E |
| AGC/008/PRZ/PRZ/APA/ABB/EPT | Transparent Glass PRZ | White ABB | ATHLON PLUS Red | Cosmos Grey AGC | EPT - Plug type E |
| ABB/001/PRZ/MGA/APA/ABB/EPT | Milk Glass MGA | White ABB | ATHLON PLUS Blue | White ABB | EPT - Plug type E |
| AGC/001/PRZ/MGA/APA/ABB/EPT | Milk Glass MGA | White ABB | ATHLON PLUS Blue | Cosmos Grey AGC | EPT - Plug type E |
| ABB/002/PRZ/MGA/APA/ABB/EPT | Milk Glass MGA | White ABB | ATHLON PLUS Dark grey | White ABB | EPT - Plug type E |
| AGC/002/PRZ/MGA/APA/ABB/EPT | Milk Glass MGA | White ABB | ATHLON PLUS Dark grey | Cosmos Grey AGC | EPT - Plug type E |
| ABB/003/PRZ/MGA/APA/ABB/EPT | Milk Glass MGA | White ABB | ATHLON PLUS Light grey | White ABB | EPT - Plug type E |
| AGC/003/PRZ/MGA/APA/ABB/EPT | Milk Glass MGA | White ABB | ATHLON PLUS Light grey | Cosmos Grey AGC | EPT - Plug type E |
| ABB/004/PRZ/MGA/APA/ABB/EPT | Milk Glass MGA | White ABB | ATHLON PLUS Light green | White ABB | EPT - Plug type E |
| AGC/004/PRZ/MGA/APA/ABB/EPT | Milk Glass MGA | White ABB | ATHLON PLUS Light green | Cosmos Grey AGC | EPT - Plug type E |
| ABB/005/PRZ/MGA/APA/ABB/EPT | Milk Glass MGA | White ABB | ATHLON PLUS Yellow | White ABB | EPT - Plug type E |
| AGC/005/PRZ/MGA/APA/ABB/EPT | Milk Glass MGA | White ABB | ATHLON PLUS Yellow | Cosmos Grey AGC | EPT - Plug type E |
| ABB/006/PRZ/MGA/APA/ABB/EPT | Milk Glass MGA | White ABB | ATHLON PLUS Orange | White ABB | EPT - Plug type E |
| AGC/006/PRZ/MGA/APA/ABB/EPT | Milk Glass MGA | White ABB | ATHLON PLUS Orange | Cosmos Grey AGC | EPT - Plug type E |
| ABB/007/PRZ/MGA/APA/ABB/EPT | Milk Glass MGA | White ABB | ATHLON PLUS Beige | White ABB | EPT - Plug type E |
| AGC/007/PRZ/MGA/APA/ABB/EPT | Milk Glass MGA | White ABB | ATHLON PLUS Beige | Cosmos Grey AGC | EPT - Plug type E |
| ABB/008/PRZ/MGA/APA/ABB/EPT | Milk Glass MGA | White ABB | ATHLON PLUS Red | White ABB | EPT - Plug type E |
| AGC/008/PRZ/MGA/APA/ABB/EPT | Milk Glass MGA | White ABB | ATHLON PLUS Red | Cosmos Grey AGC | EPT - Plug type E |
| ABB/001/PRZ/PRZ/EUR/AGA/EPT | Transparent Glass PRZ | Velvet Black AGA | ATHLON PLUS Blue | White ABB | EPT - Plug type E |
| AGC/001/PRZ/PRZ/EUR/AGA/EPT | Transparent Glass PRZ | Velvet Black AGA | ATHLON PLUS Blue | Cosmos Grey AGC | EPT - Plug type E |
| ABB/002/PRZ/PRZ/EUR/AGA/EPT | Transparent Glass PRZ | Velvet Black AGA | ATHLON PLUS Dark grey | White ABB | EPT - Plug type E |
| AGC/002/PRZ/PRZ/EUR/AGA/EPT | Transparent Glass PRZ | Velvet Black AGA | ATHLON PLUS Dark grey | Cosmos Grey AGC | EPT - Plug type E |
| ABB/003/PRZ/PRZ/EUR/AGA/EPT | Transparent Glass PRZ | Velvet Black AGA | ATHLON PLUS Light grey | White ABB | EPT - Plug type E |
| AGC/003/PRZ/PRZ/EUR/AGA/EPT | Transparent Glass PRZ | Velvet Black AGA | ATHLON PLUS Light grey | Cosmos Grey AGC | EPT - Plug type E |
| ABB/004/PRZ/PRZ/EUR/AGA/EPT | Transparent Glass PRZ | Velvet Black AGA | ATHLON PLUS Light green | White ABB | EPT - Plug type E |
| AGC/004/PRZ/PRZ/EUR/AGA/EPT | Transparent Glass PRZ | Velvet Black AGA | ATHLON PLUS Light green | Cosmos Grey AGC | EPT - Plug type E |
| ABB/005/PRZ/PRZ/EUR/AGA/EPT | Transparent Glass PRZ | Velvet Black AGA | ATHLON PLUS Yellow | White ABB | EPT - Plug type E |
| AGC/005/PRZ/PRZ/EUR/AGA/EPT | Transparent Glass PRZ | Velvet Black AGA | ATHLON PLUS Yellow | Cosmos Grey AGC | EPT - Plug type E |
| ABB/006/PRZ/PRZ/EUR/AGA/EPT | Transparent Glass PRZ | Velvet Black AGA | ATHLON PLUS Orange | White ABB | EPT - Plug type E |
| AGC/006/PRZ/PRZ/EUR/AGA/EPT | Transparent Glass PRZ | Velvet Black AGA | ATHLON PLUS Orange | Cosmos Grey AGC | EPT - Plug type E |
| ABB/007/PRZ/PRZ/EUR/AGA/EPT | Transparent Glass PRZ | Velvet Black AGA | ATHLON PLUS Beige | White ABB | EPT - Plug type E |
| AGC/007/PRZ/PRZ/EUR/AGA/EPT | Transparent Glass PRZ | Velvet Black AGA | ATHLON PLUS Beige | Cosmos Grey AGC | EPT - Plug type E |
| ABB/008/PRZ/PRZ/EUR/AGA/EPT | Transparent Glass PRZ | Velvet Black AGA | ATHLON PLUS Red | White ABB | EPT - Plug type E |
| AGC/008/PRZ/PRZ/EUR/AGA/EPT | Transparent Glass PRZ | Velvet Black AGA | ATHLON PLUS Red | Cosmos Grey AGC | EPT - Plug type E |
| ABB/001/PRZ/MGA/EUR/AGA/EPT | Milk Glass MGA | Velvet Black AGA | ATHLON PLUS Blue | White ABB | EPT - Plug type E |
| AGC/001/PRZ/MGA/EUR/AGA/EPT | Milk Glass MGA | Velvet Black AGA | ATHLON PLUS Blue | Cosmos Grey AGC | EPT - Plug type E |
| ABB/002/PRZ/MGA/EUR/AGA/EPT | Milk Glass MGA | Velvet Black AGA | ATHLON PLUS Dark grey | White ABB | EPT - Plug type E |
| AGC/002/PRZ/MGA/EUR/AGA/EPT | Milk Glass MGA | Velvet Black AGA | ATHLON PLUS Dark grey | Cosmos Grey AGC | EPT - Plug type E |
| ABB/003/PRZ/MGA/EUR/AGA/EPT | Milk Glass MGA | Velvet Black AGA | ATHLON PLUS Light grey | White ABB | EPT - Plug type E |
| AGC/003/PRZ/MGA/EUR/AGA/EPT | Milk Glass MGA | Velvet Black AGA | ATHLON PLUS Light grey | Cosmos Grey AGC | EPT - Plug type E |
| ABB/004/PRZ/MGA/EUR/AGA/EPT | Milk Glass MGA | Velvet Black AGA | ATHLON PLUS Light green | White ABB | EPT - Plug type E |
| AGC/004/PRZ/MGA/EUR/AGA/EPT | Milk Glass MGA | Velvet Black AGA | ATHLON PLUS Light green | Cosmos Grey AGC | EPT - Plug type E |
| ABB/005/PRZ/MGA/EUR/AGA/EPT | Milk Glass MGA | Velvet Black AGA | ATHLON PLUS Yellow | White ABB | EPT - Plug type E |
| AGC/005/PRZ/MGA/EUR/AGA/EPT | Milk Glass MGA | Velvet Black AGA | ATHLON PLUS Yellow | Cosmos Grey AGC | EPT - Plug type E |
| ABB/006/PRZ/MGA/EUR/AGA/EPT | Milk Glass MGA | Velvet Black AGA | ATHLON PLUS Orange | White ABB | EPT - Plug type E |
| AGC/006/PRZ/MGA/EUR/AGA/EPT | Milk Glass MGA | Velvet Black AGA | ATHLON PLUS Orange | Cosmos Grey AGC | EPT - Plug type E |
| ABB/007/PRZ/MGA/EUR/AGA/EPT | Milk Glass MGA | Velvet Black AGA | ATHLON PLUS Beige | White ABB | EPT - Plug type E |
| AGC/007/PRZ/MGA/EUR/AGA/EPT | Milk Glass MGA | Velvet Black AGA | ATHLON PLUS Beige | Cosmos Grey AGC | EPT - Plug type E |
| ABB/008/PRZ/MGA/EUR/AGA/EPT | Milk Glass MGA | Velvet Black AGA | ATHLON PLUS Red | White ABB | EPT - Plug type E |
| AGC/008/PRZ/MGA/EUR/AGA/EPT | Milk Glass MGA | Velvet Black AGA | ATHLON PLUS Red | Cosmos Grey AGC | EPT - Plug type E |
| ABB/001/PRZ/PRZ/APA/AGA/EPT | Transparent Glass PRZ | Velvet Black AGA | ATHLON PLUS Blue | White ABB | EPT - Plug type E |
| AGC/001/PRZ/PRZ/APA/AGA/EPT | Transparent Glass PRZ | Velvet Black AGA | ATHLON PLUS Blue | Cosmos Grey AGC | EPT - Plug type E |
| ABB/002/PRZ/PRZ/APA/AGA/EPT | Transparent Glass PRZ | Velvet Black AGA | ATHLON PLUS Dark grey | White ABB | EPT - Plug type E |
| AGC/002/PRZ/PRZ/APA/AGA/EPT | Transparent Glass PRZ | Velvet Black AGA | ATHLON PLUS Dark grey | Cosmos Grey AGC | EPT - Plug type E |
| ABB/003/PRZ/PRZ/APA/AGA/EPT | Transparent Glass PRZ | Velvet Black AGA | ATHLON PLUS Light grey | White ABB | EPT - Plug type E |
| AGC/003/PRZ/PRZ/APA/AGA/EPT | Transparent Glass PRZ | Velvet Black AGA | ATHLON PLUS Light grey | Cosmos Grey AGC | EPT - Plug type E |
| ABB/004/PRZ/PRZ/APA/AGA/EPT | Transparent Glass PRZ | Velvet Black AGA | ATHLON PLUS Light green | White ABB | EPT - Plug type E |
| AGC/004/PRZ/PRZ/APA/AGA/EPT | Transparent Glass PRZ | Velvet Black AGA | ATHLON PLUS Light green | Cosmos Grey AGC | EPT - Plug type E |
| ABB/005/PRZ/PRZ/APA/AGA/EPT | Transparent Glass PRZ | Velvet Black AGA | ATHLON PLUS Yellow | White ABB | EPT - Plug type E |
| AGC/005/PRZ/PRZ/APA/AGA/EPT | Transparent Glass PRZ | Velvet Black AGA | ATHLON PLUS Yellow | Cosmos Grey AGC | EPT - Plug type E |
| ABB/006/PRZ/PRZ/APA/AGA/EPT | Transparent Glass PRZ | Velvet Black AGA | ATHLON PLUS Orange | White ABB | EPT - Plug type E |
| AGC/006/PRZ/PRZ/APA/AGA/EPT | Transparent Glass PRZ | Velvet Black AGA | ATHLON PLUS Orange | Cosmos Grey AGC | EPT - Plug type E |
| ABB/007/PRZ/PRZ/APA/AGA/EPT | Transparent Glass PRZ | Velvet Black AGA | ATHLON PLUS Beige | White ABB | EPT - Plug type E |
| AGC/007/PRZ/PRZ/APA/AGA/EPT | Transparent Glass PRZ | Velvet Black AGA | ATHLON PLUS Beige | Cosmos Grey AGC | EPT - Plug type E |
| ABB/008/PRZ/PRZ/APA/AGA/EPT | Transparent Glass PRZ | Velvet Black AGA | ATHLON PLUS Red | White ABB | EPT - Plug type E |
| AGC/008/PRZ/PRZ/APA/AGA/EPT | Transparent Glass PRZ | Velvet Black AGA | ATHLON PLUS Red | Cosmos Grey AGC | EPT - Plug type E |
| ABB/001/PRZ/MGA/APA/AGA/EPT | Milk Glass MGA | Velvet Black AGA | ATHLON PLUS Blue | White ABB | EPT - Plug type E |
| AGC/001/PRZ/MGA/APA/AGA/EPT | Milk Glass MGA | Velvet Black AGA | ATHLON PLUS Blue | Cosmos Grey AGC | EPT - Plug type E |
| ABB/002/PRZ/MGA/APA/AGA/EPT | Milk Glass MGA | Velvet Black AGA | ATHLON PLUS Dark grey | White ABB | EPT - Plug type E |
| AGC/002/PRZ/MGA/APA/AGA/EPT | Milk Glass MGA | Velvet Black AGA | ATHLON PLUS Dark grey | Cosmos Grey AGC | EPT - Plug type E |
| ABB/003/PRZ/MGA/APA/AGA/EPT | Milk Glass MGA | Velvet Black AGA | ATHLON PLUS Light grey | White ABB | EPT - Plug type E |
| AGC/003/PRZ/MGA/APA/AGA/EPT | Milk Glass MGA | Velvet Black AGA | ATHLON PLUS Light grey | Cosmos Grey AGC | EPT - Plug type E |
| ABB/004/PRZ/MGA/APA/AGA/EPT | Milk Glass MGA | Velvet Black AGA | ATHLON PLUS Light green | White ABB | EPT - Plug type E |
| AGC/004/PRZ/MGA/APA/AGA/EPT | Milk Glass MGA | Velvet Black AGA | ATHLON PLUS Light green | Cosmos Grey AGC | EPT - Plug type E |
| ABB/005/PRZ/MGA/APA/AGA/EPT | Milk Glass MGA | Velvet Black AGA | ATHLON PLUS Yellow | White ABB | EPT - Plug type E |
| AGC/005/PRZ/MGA/APA/AGA/EPT | Milk Glass MGA | Velvet Black AGA | ATHLON PLUS Yellow | Cosmos Grey AGC | EPT - Plug type E |
| ABB/006/PRZ/MGA/APA/AGA/EPT | Milk Glass MGA | Velvet Black AGA | ATHLON PLUS Orange | White ABB | EPT - Plug type E |
| AGC/006/PRZ/MGA/APA/AGA/EPT | Milk Glass MGA | Velvet Black AGA | ATHLON PLUS Orange | Cosmos Grey AGC | EPT - Plug type E |
| ABB/007/PRZ/MGA/APA/AGA/EPT | Milk Glass MGA | Velvet Black AGA | ATHLON PLUS Beige | White ABB | EPT - Plug type E |
| AGC/007/PRZ/MGA/APA/AGA/EPT | Milk Glass MGA | Velvet Black AGA | ATHLON PLUS Beige | Cosmos Grey AGC | EPT - Plug type E |
| ABB/008/PRZ/MGA/APA/AGA/EPT | Milk Glass MGA | Velvet Black AGA | ATHLON PLUS Red | White ABB | EPT - Plug type E |
| AGC/008/PRZ/MGA/APA/AGA/EPT | Milk Glass MGA | Velvet Black AGA | ATHLON PLUS Red | Cosmos Grey AGC | EPT - Plug type E |
| ABB/001/PRZ/PRZ/EUR/ABB/KPT | Transparent Glass PRZ | White ABB | ATHLON PLUS Blue | White ABB | KPT - Plug type K |
| AGC/001/PRZ/PRZ/EUR/ABB/KPT | Transparent Glass PRZ | White ABB | ATHLON PLUS Blue | Cosmos Grey AGC | KPT - Plug type K |
| ABB/002/PRZ/PRZ/EUR/ABB/KPT | Transparent Glass PRZ | White ABB | ATHLON PLUS Dark grey | White ABB | KPT - Plug type K |
| AGC/002/PRZ/PRZ/EUR/ABB/KPT | Transparent Glass PRZ | White ABB | ATHLON PLUS Dark grey | Cosmos Grey AGC | KPT - Plug type K |
| ABB/003/PRZ/PRZ/EUR/ABB/KPT | Transparent Glass PRZ | White ABB | ATHLON PLUS Light grey | White ABB | KPT - Plug type K |
| AGC/003/PRZ/PRZ/EUR/ABB/KPT | Transparent Glass PRZ | White ABB | ATHLON PLUS Light grey | Cosmos Grey AGC | KPT - Plug type K |
| ABB/004/PRZ/PRZ/EUR/ABB/KPT | Transparent Glass PRZ | White ABB | ATHLON PLUS Light green | White ABB | KPT - Plug type K |
| AGC/004/PRZ/PRZ/EUR/ABB/KPT | Transparent Glass PRZ | White ABB | ATHLON PLUS Light green | Cosmos Grey AGC | KPT - Plug type K |
| ABB/005/PRZ/PRZ/EUR/ABB/KPT | Transparent Glass PRZ | White ABB | ATHLON PLUS Yellow | White ABB | KPT - Plug type K |
| AGC/005/PRZ/PRZ/EUR/ABB/KPT | Transparent Glass PRZ | White ABB | ATHLON PLUS Yellow | Cosmos Grey AGC | KPT - Plug type K |
| ABB/006/PRZ/PRZ/EUR/ABB/KPT | Transparent Glass PRZ | White ABB | ATHLON PLUS Orange | White ABB | KPT - Plug type K |
| AGC/006/PRZ/PRZ/EUR/ABB/KPT | Transparent Glass PRZ | White ABB | ATHLON PLUS Orange | Cosmos Grey AGC | KPT - Plug type K |
| ABB/007/PRZ/PRZ/EUR/ABB/KPT | Transparent Glass PRZ | White ABB | ATHLON PLUS Beige | White ABB | KPT - Plug type K |
| AGC/007/PRZ/PRZ/EUR/ABB/KPT | Transparent Glass PRZ | White ABB | ATHLON PLUS Beige | Cosmos Grey AGC | KPT - Plug type K |
| ABB/008/PRZ/PRZ/EUR/ABB/KPT | Transparent Glass PRZ | White ABB | ATHLON PLUS Red | White ABB | KPT - Plug type K |
| AGC/008/PRZ/PRZ/EUR/ABB/KPT | Transparent Glass PRZ | White ABB | ATHLON PLUS Red | Cosmos Grey AGC | KPT - Plug type K |
| ABB/001/PRZ/MGA/EUR/ABB/KPT | Milk Glass MGA | White ABB | ATHLON PLUS Blue | White ABB | KPT - Plug type K |
| AGC/001/PRZ/MGA/EUR/ABB/KPT | Milk Glass MGA | White ABB | ATHLON PLUS Blue | Cosmos Grey AGC | KPT - Plug type K |
| ABB/002/PRZ/MGA/EUR/ABB/KPT | Milk Glass MGA | White ABB | ATHLON PLUS Dark grey | White ABB | KPT - Plug type K |
| AGC/002/PRZ/MGA/EUR/ABB/KPT | Milk Glass MGA | White ABB | ATHLON PLUS Dark grey | Cosmos Grey AGC | KPT - Plug type K |
| ABB/003/PRZ/MGA/EUR/ABB/KPT | Milk Glass MGA | White ABB | ATHLON PLUS Light grey | White ABB | KPT - Plug type K |
| AGC/003/PRZ/MGA/EUR/ABB/KPT | Milk Glass MGA | White ABB | ATHLON PLUS Light grey | Cosmos Grey AGC | KPT - Plug type K |
| ABB/004/PRZ/MGA/EUR/ABB/KPT | Milk Glass MGA | White ABB | ATHLON PLUS Light green | White ABB | KPT - Plug type K |
| AGC/004/PRZ/MGA/EUR/ABB/KPT | Milk Glass MGA | White ABB | ATHLON PLUS Light green | Cosmos Grey AGC | KPT - Plug type K |
| ABB/005/PRZ/MGA/EUR/ABB/KPT | Milk Glass MGA | White ABB | ATHLON PLUS Yellow | White ABB | KPT - Plug type K |
| AGC/005/PRZ/MGA/EUR/ABB/KPT | Milk Glass MGA | White ABB | ATHLON PLUS Yellow | Cosmos Grey AGC | KPT - Plug type K |
| ABB/006/PRZ/MGA/EUR/ABB/KPT | Milk Glass MGA | White ABB | ATHLON PLUS Orange | White ABB | KPT - Plug type K |
| AGC/006/PRZ/MGA/EUR/ABB/KPT | Milk Glass MGA | White ABB | ATHLON PLUS Orange | Cosmos Grey AGC | KPT - Plug type K |
| ABB/007/PRZ/MGA/EUR/ABB/KPT | Milk Glass MGA | White ABB | ATHLON PLUS Beige | White ABB | KPT - Plug type K |
| AGC/007/PRZ/MGA/EUR/ABB/KPT | Milk Glass MGA | White ABB | ATHLON PLUS Beige | Cosmos Grey AGC | KPT - Plug type K |
| ABB/008/PRZ/MGA/EUR/ABB/KPT | Milk Glass MGA | White ABB | ATHLON PLUS Red | White ABB | KPT - Plug type K |
| AGC/008/PRZ/MGA/EUR/ABB/KPT | Milk Glass MGA | White ABB | ATHLON PLUS Red | Cosmos Grey AGC | KPT - Plug type K |
| ABB/001/PRZ/PRZ/EUR/AGA/KPT | Transparent Glass PRZ | Velvet Black AGA | ATHLON PLUS Blue | White ABB | KPT - Plug type K |
| AGC/001/PRZ/PRZ/EUR/AGA/KPT | Transparent Glass PRZ | Velvet Black AGA | ATHLON PLUS Blue | Cosmos Grey AGC | KPT - Plug type K |
| ABB/002/PRZ/PRZ/EUR/AGA/KPT | Transparent Glass PRZ | Velvet Black AGA | ATHLON PLUS Dark grey | White ABB | KPT - Plug type K |
| AGC/002/PRZ/PRZ/EUR/AGA/KPT | Transparent Glass PRZ | Velvet Black AGA | ATHLON PLUS Dark grey | Cosmos Grey AGC | KPT - Plug type K |
| ABB/003/PRZ/PRZ/EUR/AGA/KPT | Transparent Glass PRZ | Velvet Black AGA | ATHLON PLUS Light grey | White ABB | KPT - Plug type K |
| AGC/003/PRZ/PRZ/EUR/AGA/KPT | Transparent Glass PRZ | Velvet Black AGA | ATHLON PLUS Light grey | Cosmos Grey AGC | KPT - Plug type K |
| ABB/004/PRZ/PRZ/EUR/AGA/KPT | Transparent Glass PRZ | Velvet Black AGA | ATHLON PLUS Light green | White ABB | KPT - Plug type K |
| AGC/004/PRZ/PRZ/EUR/AGA/KPT | Transparent Glass PRZ | Velvet Black AGA | ATHLON PLUS Light green | Cosmos Grey AGC | KPT - Plug type K |
| ABB/005/PRZ/PRZ/EUR/AGA/KPT | Transparent Glass PRZ | Velvet Black AGA | ATHLON PLUS Yellow | White ABB | KPT - Plug type K |
| AGC/005/PRZ/PRZ/EUR/AGA/KPT | Transparent Glass PRZ | Velvet Black AGA | ATHLON PLUS Yellow | Cosmos Grey AGC | KPT - Plug type K |
| ABB/006/PRZ/PRZ/EUR/AGA/KPT | Transparent Glass PRZ | Velvet Black AGA | ATHLON PLUS Orange | White ABB | KPT - Plug type K |
| AGC/006/PRZ/PRZ/EUR/AGA/KPT | Transparent Glass PRZ | Velvet Black AGA | ATHLON PLUS Orange | Cosmos Grey AGC | KPT - Plug type K |
| ABB/007/PRZ/PRZ/EUR/AGA/KPT | Transparent Glass PRZ | Velvet Black AGA | ATHLON PLUS Beige | White ABB | KPT - Plug type K |
| AGC/007/PRZ/PRZ/EUR/AGA/KPT | Transparent Glass PRZ | Velvet Black AGA | ATHLON PLUS Beige | Cosmos Grey AGC | KPT - Plug type K |
| ABB/008/PRZ/PRZ/EUR/AGA/KPT | Transparent Glass PRZ | Velvet Black AGA | ATHLON PLUS Red | White ABB | KPT - Plug type K |
| AGC/008/PRZ/PRZ/EUR/AGA/KPT | Transparent Glass PRZ | Velvet Black AGA | ATHLON PLUS Red | Cosmos Grey AGC | KPT - Plug type K |
| ABB/001/PRZ/MGA/EUR/AGA/KPT | Milk Glass MGA | Velvet Black AGA | ATHLON PLUS Blue | White ABB | KPT - Plug type K |
| AGC/001/PRZ/MGA/EUR/AGA/KPT | Milk Glass MGA | Velvet Black AGA | ATHLON PLUS Blue | Cosmos Grey AGC | KPT - Plug type K |
| ABB/002/PRZ/MGA/EUR/AGA/KPT | Milk Glass MGA | Velvet Black AGA | ATHLON PLUS Dark grey | White ABB | KPT - Plug type K |
| AGC/002/PRZ/MGA/EUR/AGA/KPT | Milk Glass MGA | Velvet Black AGA | ATHLON PLUS Dark grey | Cosmos Grey AGC | KPT - Plug type K |
| ABB/003/PRZ/MGA/EUR/AGA/KPT | Milk Glass MGA | Velvet Black AGA | ATHLON PLUS Light grey | White ABB | KPT - Plug type K |
| AGC/003/PRZ/MGA/EUR/AGA/KPT | Milk Glass MGA | Velvet Black AGA | ATHLON PLUS Light grey | Cosmos Grey AGC | KPT - Plug type K |
| ABB/004/PRZ/MGA/EUR/AGA/KPT | Milk Glass MGA | Velvet Black AGA | ATHLON PLUS Light green | White ABB | KPT - Plug type K |
| AGC/004/PRZ/MGA/EUR/AGA/KPT | Milk Glass MGA | Velvet Black AGA | ATHLON PLUS Light green | Cosmos Grey AGC | KPT - Plug type K |
| ABB/005/PRZ/MGA/EUR/AGA/KPT | Milk Glass MGA | Velvet Black AGA | ATHLON PLUS Yellow | White ABB | KPT - Plug type K |
| AGC/005/PRZ/MGA/EUR/AGA/KPT | Milk Glass MGA | Velvet Black AGA | ATHLON PLUS Yellow | Cosmos Grey AGC | KPT - Plug type K |
| ABB/006/PRZ/MGA/EUR/AGA/KPT | Milk Glass MGA | Velvet Black AGA | ATHLON PLUS Orange | White ABB | KPT - Plug type K |
| AGC/006/PRZ/MGA/EUR/AGA/KPT | Milk Glass MGA | Velvet Black AGA | ATHLON PLUS Orange | Cosmos Grey AGC | KPT - Plug type K |
| ABB/007/PRZ/MGA/EUR/AGA/KPT | Milk Glass MGA | Velvet Black AGA | ATHLON PLUS Beige | White ABB | KPT - Plug type K |
| AGC/007/PRZ/MGA/EUR/AGA/KPT | Milk Glass MGA | Velvet Black AGA | ATHLON PLUS Beige | Cosmos Grey AGC | KPT - Plug type K |
| ABB/008/PRZ/MGA/EUR/AGA/KPT | Milk Glass MGA | Velvet Black AGA | ATHLON PLUS Red | White ABB | KPT - Plug type K |
| AGC/008/PRZ/MGA/EUR/AGA/KPT | Milk Glass MGA | Velvet Black AGA | ATHLON PLUS Red | Cosmos Grey AGC | KPT - Plug type K |
| ABB/001/PRZ/PRZ/EUR/ABB/JPT | Transparent Glass PRZ | White ABB | ATHLON PLUS Blue | White ABB | JPT - Plug type J |
| AGC/001/PRZ/PRZ/EUR/ABB/JPT | Transparent Glass PRZ | White ABB | ATHLON PLUS Blue | Cosmos Grey AGC | JPT - Plug type J |
| ABB/002/PRZ/PRZ/EUR/ABB/JPT | Transparent Glass PRZ | White ABB | ATHLON PLUS Dark grey | White ABB | JPT - Plug type J |
| AGC/002/PRZ/PRZ/EUR/ABB/JPT | Transparent Glass PRZ | White ABB | ATHLON PLUS Dark grey | Cosmos Grey AGC | JPT - Plug type J |
| ABB/003/PRZ/PRZ/EUR/ABB/JPT | Transparent Glass PRZ | White ABB | ATHLON PLUS Light grey | White ABB | JPT - Plug type J |
| AGC/003/PRZ/PRZ/EUR/ABB/JPT | Transparent Glass PRZ | White ABB | ATHLON PLUS Light grey | Cosmos Grey AGC | JPT - Plug type J |
| ABB/004/PRZ/PRZ/EUR/ABB/JPT | Transparent Glass PRZ | White ABB | ATHLON PLUS Light green | White ABB | JPT - Plug type J |
| AGC/004/PRZ/PRZ/EUR/ABB/JPT | Transparent Glass PRZ | White ABB | ATHLON PLUS Light green | Cosmos Grey AGC | JPT - Plug type J |
| ABB/005/PRZ/PRZ/EUR/ABB/JPT | Transparent Glass PRZ | White ABB | ATHLON PLUS Yellow | White ABB | JPT - Plug type J |
| AGC/005/PRZ/PRZ/EUR/ABB/JPT | Transparent Glass PRZ | White ABB | ATHLON PLUS Yellow | Cosmos Grey AGC | JPT - Plug type J |
| ABB/006/PRZ/PRZ/EUR/ABB/JPT | Transparent Glass PRZ | White ABB | ATHLON PLUS Orange | White ABB | JPT - Plug type J |
| AGC/006/PRZ/PRZ/EUR/ABB/JPT | Transparent Glass PRZ | White ABB | ATHLON PLUS Orange | Cosmos Grey AGC | JPT - Plug type J |
| ABB/007/PRZ/PRZ/EUR/ABB/JPT | Transparent Glass PRZ | White ABB | ATHLON PLUS Beige | White ABB | JPT - Plug type J |
| AGC/007/PRZ/PRZ/EUR/ABB/JPT | Transparent Glass PRZ | White ABB | ATHLON PLUS Beige | Cosmos Grey AGC | JPT - Plug type J |
| ABB/008/PRZ/PRZ/EUR/ABB/JPT | Transparent Glass PRZ | White ABB | ATHLON PLUS Red | White ABB | JPT - Plug type J |
| AGC/008/PRZ/PRZ/EUR/ABB/JPT | Transparent Glass PRZ | White ABB | ATHLON PLUS Red | Cosmos Grey AGC | JPT - Plug type J |
| ABB/001/PRZ/MGA/EUR/ABB/JPT | Milk Glass MGA | White ABB | ATHLON PLUS Blue | White ABB | JPT - Plug type J |
| AGC/001/PRZ/MGA/EUR/ABB/JPT | Milk Glass MGA | White ABB | ATHLON PLUS Blue | Cosmos Grey AGC | JPT - Plug type J |
| ABB/002/PRZ/MGA/EUR/ABB/JPT | Milk Glass MGA | White ABB | ATHLON PLUS Dark grey | White ABB | JPT - Plug type J |
| AGC/002/PRZ/MGA/EUR/ABB/JPT | Milk Glass MGA | White ABB | ATHLON PLUS Dark grey | Cosmos Grey AGC | JPT - Plug type J |
| ABB/003/PRZ/MGA/EUR/ABB/JPT | Milk Glass MGA | White ABB | ATHLON PLUS Light grey | White ABB | JPT - Plug type J |
| AGC/003/PRZ/MGA/EUR/ABB/JPT | Milk Glass MGA | White ABB | ATHLON PLUS Light grey | Cosmos Grey AGC | JPT - Plug type J |
| ABB/004/PRZ/MGA/EUR/ABB/JPT | Milk Glass MGA | White ABB | ATHLON PLUS Light green | White ABB | JPT - Plug type J |
| AGC/004/PRZ/MGA/EUR/ABB/JPT | Milk Glass MGA | White ABB | ATHLON PLUS Light green | Cosmos Grey AGC | JPT - Plug type J |
| ABB/005/PRZ/MGA/EUR/ABB/JPT | Milk Glass MGA | White ABB | ATHLON PLUS Yellow | White ABB | JPT - Plug type J |
| AGC/005/PRZ/MGA/EUR/ABB/JPT | Milk Glass MGA | White ABB | ATHLON PLUS Yellow | Cosmos Grey AGC | JPT - Plug type J |
| ABB/006/PRZ/MGA/EUR/ABB/JPT | Milk Glass MGA | White ABB | ATHLON PLUS Orange | White ABB | JPT - Plug type J |
| AGC/006/PRZ/MGA/EUR/ABB/JPT | Milk Glass MGA | White ABB | ATHLON PLUS Orange | Cosmos Grey AGC | JPT - Plug type J |
| ABB/007/PRZ/MGA/EUR/ABB/JPT | Milk Glass MGA | White ABB | ATHLON PLUS Beige | White ABB | JPT - Plug type J |
| AGC/007/PRZ/MGA/EUR/ABB/JPT | Milk Glass MGA | White ABB | ATHLON PLUS Beige | Cosmos Grey AGC | JPT - Plug type J |
| ABB/008/PRZ/MGA/EUR/ABB/JPT | Milk Glass MGA | White ABB | ATHLON PLUS Red | White ABB | JPT - Plug type J |
| AGC/008/PRZ/MGA/EUR/ABB/JPT | Milk Glass MGA | White ABB | ATHLON PLUS Red | Cosmos Grey AGC | JPT - Plug type J |
| ABB/001/PRZ/PRZ/EUR/AGA/JPT | Transparent Glass PRZ | Velvet Black AGA | ATHLON PLUS Blue | White ABB | JPT - Plug type J |
| AGC/001/PRZ/PRZ/EUR/AGA/JPT | Transparent Glass PRZ | Velvet Black AGA | ATHLON PLUS Blue | Cosmos Grey AGC | JPT - Plug type J |
| ABB/002/PRZ/PRZ/EUR/AGA/JPT | Transparent Glass PRZ | Velvet Black AGA | ATHLON PLUS Dark grey | White ABB | JPT - Plug type J |
| AGC/002/PRZ/PRZ/EUR/AGA/JPT | Transparent Glass PRZ | Velvet Black AGA | ATHLON PLUS Dark grey | Cosmos Grey AGC | JPT - Plug type J |
| ABB/003/PRZ/PRZ/EUR/AGA/JPT | Transparent Glass PRZ | Velvet Black AGA | ATHLON PLUS Light grey | White ABB | JPT - Plug type J |
| AGC/003/PRZ/PRZ/EUR/AGA/JPT | Transparent Glass PRZ | Velvet Black AGA | ATHLON PLUS Light grey | Cosmos Grey AGC | JPT - Plug type J |
| ABB/004/PRZ/PRZ/EUR/AGA/JPT | Transparent Glass PRZ | Velvet Black AGA | ATHLON PLUS Light green | White ABB | JPT - Plug type J |
| AGC/004/PRZ/PRZ/EUR/AGA/JPT | Transparent Glass PRZ | Velvet Black AGA | ATHLON PLUS Light green | Cosmos Grey AGC | JPT - Plug type J |
| ABB/005/PRZ/PRZ/EUR/AGA/JPT | Transparent Glass PRZ | Velvet Black AGA | ATHLON PLUS Yellow | White ABB | JPT - Plug type J |
| AGC/005/PRZ/PRZ/EUR/AGA/JPT | Transparent Glass PRZ | Velvet Black AGA | ATHLON PLUS Yellow | Cosmos Grey AGC | JPT - Plug type J |
| ABB/006/PRZ/PRZ/EUR/AGA/JPT | Transparent Glass PRZ | Velvet Black AGA | ATHLON PLUS Orange | White ABB | JPT - Plug type J |
| AGC/006/PRZ/PRZ/EUR/AGA/JPT | Transparent Glass PRZ | Velvet Black AGA | ATHLON PLUS Orange | Cosmos Grey AGC | JPT - Plug type J |
| ABB/007/PRZ/PRZ/EUR/AGA/JPT | Transparent Glass PRZ | Velvet Black AGA | ATHLON PLUS Beige | White ABB | JPT - Plug type J |
| AGC/007/PRZ/PRZ/EUR/AGA/JPT | Transparent Glass PRZ | Velvet Black AGA | ATHLON PLUS Beige | Cosmos Grey AGC | JPT - Plug type J |
| ABB/008/PRZ/PRZ/EUR/AGA/JPT | Transparent Glass PRZ | Velvet Black AGA | ATHLON PLUS Red | White ABB | JPT - Plug type J |
| AGC/008/PRZ/PRZ/EUR/AGA/JPT | Transparent Glass PRZ | Velvet Black AGA | ATHLON PLUS Red | Cosmos Grey AGC | JPT - Plug type J |
| ABB/001/PRZ/MGA/EUR/AGA/JPT | Milk Glass MGA | Velvet Black AGA | ATHLON PLUS Blue | White ABB | JPT - Plug type J |
| AGC/001/PRZ/MGA/EUR/AGA/JPT | Milk Glass MGA | Velvet Black AGA | ATHLON PLUS Blue | Cosmos Grey AGC | JPT - Plug type J |
| ABB/002/PRZ/MGA/EUR/AGA/JPT | Milk Glass MGA | Velvet Black AGA | ATHLON PLUS Dark grey | White ABB | JPT - Plug type J |
| AGC/002/PRZ/MGA/EUR/AGA/JPT | Milk Glass MGA | Velvet Black AGA | ATHLON PLUS Dark grey | Cosmos Grey AGC | JPT - Plug type J |
| ABB/003/PRZ/MGA/EUR/AGA/JPT | Milk Glass MGA | Velvet Black AGA | ATHLON PLUS Light grey | White ABB | JPT - Plug type J |
| AGC/003/PRZ/MGA/EUR/AGA/JPT | Milk Glass MGA | Velvet Black AGA | ATHLON PLUS Light grey | Cosmos Grey AGC | JPT - Plug type J |
| ABB/004/PRZ/MGA/EUR/AGA/JPT | Milk Glass MGA | Velvet Black AGA | ATHLON PLUS Light green | White ABB | JPT - Plug type J |
| AGC/004/PRZ/MGA/EUR/AGA/JPT | Milk Glass MGA | Velvet Black AGA | ATHLON PLUS Light green | Cosmos Grey AGC | JPT - Plug type J |
| ABB/005/PRZ/MGA/EUR/AGA/JPT | Milk Glass MGA | Velvet Black AGA | ATHLON PLUS Yellow | White ABB | JPT - Plug type J |
| AGC/005/PRZ/MGA/EUR/AGA/JPT | Milk Glass MGA | Velvet Black AGA | ATHLON PLUS Yellow | Cosmos Grey AGC | JPT - Plug type J |
| ABB/006/PRZ/MGA/EUR/AGA/JPT | Milk Glass MGA | Velvet Black AGA | ATHLON PLUS Orange | White ABB | JPT - Plug type J |
| AGC/006/PRZ/MGA/EUR/AGA/JPT | Milk Glass MGA | Velvet Black AGA | ATHLON PLUS Orange | Cosmos Grey AGC | JPT - Plug type J |
| ABB/007/PRZ/MGA/EUR/AGA/JPT | Milk Glass MGA | Velvet Black AGA | ATHLON PLUS Beige | White ABB | JPT - Plug type J |
| AGC/007/PRZ/MGA/EUR/AGA/JPT | Milk Glass MGA | Velvet Black AGA | ATHLON PLUS Beige | Cosmos Grey AGC | JPT - Plug type J |
| ABB/008/PRZ/MGA/EUR/AGA/JPT | Milk Glass MGA | Velvet Black AGA | ATHLON PLUS Red | White ABB | JPT - Plug type J |
| AGC/008/PRZ/MGA/EUR/AGA/JPT | Milk Glass MGA | Velvet Black AGA | ATHLON PLUS Red | Cosmos Grey AGC | JPT - Plug type J |
| ABB/001/PRZ/PRZ/APA/ABB/CPT | Transparent Glass PRZ | White ABB | ATHLON PLUS Blue | White ABB | CPT - Plug type CNC |
| AGC/001/PRZ/PRZ/APA/ABB/CPT | Transparent Glass PRZ | White ABB | ATHLON PLUS Blue | Cosmos Grey AGC | CPT - Plug type CNC |
| ABB/002/PRZ/PRZ/APA/ABB/CPT | Transparent Glass PRZ | White ABB | ATHLON PLUS Dark grey | White ABB | CPT - Plug type CNC |
| AGC/002/PRZ/PRZ/APA/ABB/CPT | Transparent Glass PRZ | White ABB | ATHLON PLUS Dark grey | Cosmos Grey AGC | CPT - Plug type CNC |
| ABB/003/PRZ/PRZ/APA/ABB/CPT | Transparent Glass PRZ | White ABB | ATHLON PLUS Light grey | White ABB | CPT - Plug type CNC |
| AGC/003/PRZ/PRZ/APA/ABB/CPT | Transparent Glass PRZ | White ABB | ATHLON PLUS Light grey | Cosmos Grey AGC | CPT - Plug type CNC |
| ABB/004/PRZ/PRZ/APA/ABB/CPT | Transparent Glass PRZ | White ABB | ATHLON PLUS Light green | White ABB | CPT - Plug type CNC |
| AGC/004/PRZ/PRZ/APA/ABB/CPT | Transparent Glass PRZ | White ABB | ATHLON PLUS Light green | Cosmos Grey AGC | CPT - Plug type CNC |
| ABB/005/PRZ/PRZ/APA/ABB/CPT | Transparent Glass PRZ | White ABB | ATHLON PLUS Yellow | White ABB | CPT - Plug type CNC |
| AGC/005/PRZ/PRZ/APA/ABB/CPT | Transparent Glass PRZ | White ABB | ATHLON PLUS Yellow | Cosmos Grey AGC | CPT - Plug type CNC |
| ABB/006/PRZ/PRZ/APA/ABB/CPT | Transparent Glass PRZ | White ABB | ATHLON PLUS Orange | White ABB | CPT - Plug type CNC |
| AGC/006/PRZ/PRZ/APA/ABB/CPT | Transparent Glass PRZ | White ABB | ATHLON PLUS Orange | Cosmos Grey AGC | CPT - Plug type CNC |
| ABB/007/PRZ/PRZ/APA/ABB/CPT | Transparent Glass PRZ | White ABB | ATHLON PLUS Beige | White ABB | CPT - Plug type CNC |
| AGC/007/PRZ/PRZ/APA/ABB/CPT | Transparent Glass PRZ | White ABB | ATHLON PLUS Beige | Cosmos Grey AGC | CPT - Plug type CNC |
| ABB/008/PRZ/PRZ/APA/ABB/CPT | Transparent Glass PRZ | White ABB | ATHLON PLUS Red | White ABB | CPT - Plug type CNC |
| AGC/008/PRZ/PRZ/APA/ABB/CPT | Transparent Glass PRZ | White ABB | ATHLON PLUS Red | Cosmos Grey AGC | CPT - Plug type CNC |
| ABB/001/PRZ/MGA/APA/ABB/CPT | Milk Glass MGA | White ABB | ATHLON PLUS Blue | White ABB | CPT - Plug type CNC |
| AGC/001/PRZ/MGA/APA/ABB/CPT | Milk Glass MGA | White ABB | ATHLON PLUS Blue | Cosmos Grey AGC | CPT - Plug type CNC |
| ABB/002/PRZ/MGA/APA/ABB/CPT | Milk Glass MGA | White ABB | ATHLON PLUS Dark grey | White ABB | CPT - Plug type CNC |
| AGC/002/PRZ/MGA/APA/ABB/CPT | Milk Glass MGA | White ABB | ATHLON PLUS Dark grey | Cosmos Grey AGC | CPT - Plug type CNC |
| ABB/003/PRZ/MGA/APA/ABB/CPT | Milk Glass MGA | White ABB | ATHLON PLUS Light grey | White ABB | CPT - Plug type CNC |
| AGC/003/PRZ/MGA/APA/ABB/CPT | Milk Glass MGA | White ABB | ATHLON PLUS Light grey | Cosmos Grey AGC | CPT - Plug type CNC |
| ABB/004/PRZ/MGA/APA/ABB/CPT | Milk Glass MGA | White ABB | ATHLON PLUS Light green | White ABB | CPT - Plug type CNC |
| AGC/004/PRZ/MGA/APA/ABB/CPT | Milk Glass MGA | White ABB | ATHLON PLUS Light green | Cosmos Grey AGC | CPT - Plug type CNC |
| ABB/005/PRZ/MGA/APA/ABB/CPT | Milk Glass MGA | White ABB | ATHLON PLUS Yellow | White ABB | CPT - Plug type CNC |
| AGC/005/PRZ/MGA/APA/ABB/CPT | Milk Glass MGA | White ABB | ATHLON PLUS Yellow | Cosmos Grey AGC | CPT - Plug type CNC |
| ABB/006/PRZ/MGA/APA/ABB/CPT | Milk Glass MGA | White ABB | ATHLON PLUS Orange | White ABB | CPT - Plug type CNC |
| AGC/006/PRZ/MGA/APA/ABB/CPT | Milk Glass MGA | White ABB | ATHLON PLUS Orange | Cosmos Grey AGC | CPT - Plug type CNC |
| ABB/007/PRZ/MGA/APA/ABB/CPT | Milk Glass MGA | White ABB | ATHLON PLUS Beige | White ABB | CPT - Plug type CNC |
| AGC/007/PRZ/MGA/APA/ABB/CPT | Milk Glass MGA | White ABB | ATHLON PLUS Beige | Cosmos Grey AGC | CPT - Plug type CNC |
| ABB/008/PRZ/MGA/APA/ABB/CPT | Milk Glass MGA | White ABB | ATHLON PLUS Red | White ABB | CPT - Plug type CNC |
| AGC/008/PRZ/MGA/APA/ABB/CPT | Milk Glass MGA | White ABB | ATHLON PLUS Red | Cosmos Grey AGC | CPT - Plug type CNC |
| ABB/001/PRZ/PRZ/APA/AGA/CPT | Transparent Glass PRZ | Velvet Black AGA | ATHLON PLUS Blue | White ABB | CPT - Plug type CNC |
| AGC/001/PRZ/PRZ/APA/AGA/CPT | Transparent Glass PRZ | Velvet Black AGA | ATHLON PLUS Blue | Cosmos Grey AGC | CPT - Plug type CNC |
| ABB/002/PRZ/PRZ/APA/AGA/CPT | Transparent Glass PRZ | Velvet Black AGA | ATHLON PLUS Dark grey | White ABB | CPT - Plug type CNC |
| AGC/002/PRZ/PRZ/APA/AGA/CPT | Transparent Glass PRZ | Velvet Black AGA | ATHLON PLUS Dark grey | Cosmos Grey AGC | CPT - Plug type CNC |
| ABB/003/PRZ/PRZ/APA/AGA/CPT | Transparent Glass PRZ | Velvet Black AGA | ATHLON PLUS Light grey | White ABB | CPT - Plug type CNC |
| AGC/003/PRZ/PRZ/APA/AGA/CPT | Transparent Glass PRZ | Velvet Black AGA | ATHLON PLUS Light grey | Cosmos Grey AGC | CPT - Plug type CNC |
| ABB/004/PRZ/PRZ/APA/AGA/CPT | Transparent Glass PRZ | Velvet Black AGA | ATHLON PLUS Light green | White ABB | CPT - Plug type CNC |
| AGC/004/PRZ/PRZ/APA/AGA/CPT | Transparent Glass PRZ | Velvet Black AGA | ATHLON PLUS Light green | Cosmos Grey AGC | CPT - Plug type CNC |
| ABB/005/PRZ/PRZ/APA/AGA/CPT | Transparent Glass PRZ | Velvet Black AGA | ATHLON PLUS Yellow | White ABB | CPT - Plug type CNC |
| AGC/005/PRZ/PRZ/APA/AGA/CPT | Transparent Glass PRZ | Velvet Black AGA | ATHLON PLUS Yellow | Cosmos Grey AGC | CPT - Plug type CNC |
| ABB/006/PRZ/PRZ/APA/AGA/CPT | Transparent Glass PRZ | Velvet Black AGA | ATHLON PLUS Orange | White ABB | CPT - Plug type CNC |
| AGC/006/PRZ/PRZ/APA/AGA/CPT | Transparent Glass PRZ | Velvet Black AGA | ATHLON PLUS Orange | Cosmos Grey AGC | CPT - Plug type CNC |
| ABB/007/PRZ/PRZ/APA/AGA/CPT | Transparent Glass PRZ | Velvet Black AGA | ATHLON PLUS Beige | White ABB | CPT - Plug type CNC |
| AGC/007/PRZ/PRZ/APA/AGA/CPT | Transparent Glass PRZ | Velvet Black AGA | ATHLON PLUS Beige | Cosmos Grey AGC | CPT - Plug type CNC |
| ABB/008/PRZ/PRZ/APA/AGA/CPT | Transparent Glass PRZ | Velvet Black AGA | ATHLON PLUS Red | White ABB | CPT - Plug type CNC |
| AGC/008/PRZ/PRZ/APA/AGA/CPT | Transparent Glass PRZ | Velvet Black AGA | ATHLON PLUS Red | Cosmos Grey AGC | CPT - Plug type CNC |
| ABB/001/PRZ/MGA/APA/AGA/CPT | Milk Glass MGA | Velvet Black AGA | ATHLON PLUS Blue | White ABB | CPT - Plug type CNC |
| AGC/001/PRZ/MGA/APA/AGA/CPT | Milk Glass MGA | Velvet Black AGA | ATHLON PLUS Blue | Cosmos Grey AGC | CPT - Plug type CNC |
| ABB/002/PRZ/MGA/APA/AGA/CPT | Milk Glass MGA | Velvet Black AGA | ATHLON PLUS Dark grey | White ABB | CPT - Plug type CNC |
| AGC/002/PRZ/MGA/APA/AGA/CPT | Milk Glass MGA | Velvet Black AGA | ATHLON PLUS Dark grey | Cosmos Grey AGC | CPT - Plug type CNC |
| ABB/003/PRZ/MGA/APA/AGA/CPT | Milk Glass MGA | Velvet Black AGA | ATHLON PLUS Light grey | White ABB | CPT - Plug type CNC |
| AGC/003/PRZ/MGA/APA/AGA/CPT | Milk Glass MGA | Velvet Black AGA | ATHLON PLUS Light grey | Cosmos Grey AGC | CPT - Plug type CNC |
| ABB/004/PRZ/MGA/APA/AGA/CPT | Milk Glass MGA | Velvet Black AGA | ATHLON PLUS Light green | White ABB | CPT - Plug type CNC |
| AGC/004/PRZ/MGA/APA/AGA/CPT | Milk Glass MGA | Velvet Black AGA | ATHLON PLUS Light green | Cosmos Grey AGC | CPT - Plug type CNC |
| ABB/005/PRZ/MGA/APA/AGA/CPT | Milk Glass MGA | Velvet Black AGA | ATHLON PLUS Yellow | White ABB | CPT - Plug type CNC |
| AGC/005/PRZ/MGA/APA/AGA/CPT | Milk Glass MGA | Velvet Black AGA | ATHLON PLUS Yellow | Cosmos Grey AGC | CPT - Plug type CNC |
| ABB/006/PRZ/MGA/APA/AGA/CPT | Milk Glass MGA | Velvet Black AGA | ATHLON PLUS Orange | White ABB | CPT - Plug type CNC |
| AGC/006/PRZ/MGA/APA/AGA/CPT | Milk Glass MGA | Velvet Black AGA | ATHLON PLUS Orange | Cosmos Grey AGC | CPT - Plug type CNC |
| ABB/007/PRZ/MGA/APA/AGA/CPT | Milk Glass MGA | Velvet Black AGA | ATHLON PLUS Beige | White ABB | CPT - Plug type CNC |
| AGC/007/PRZ/MGA/APA/AGA/CPT | Milk Glass MGA | Velvet Black AGA | ATHLON PLUS Beige | Cosmos Grey AGC | CPT - Plug type CNC |
| ABB/008/PRZ/MGA/APA/AGA/CPT | Milk Glass MGA | Velvet Black AGA | ATHLON PLUS Red | White ABB | CPT - Plug type CNC |
| AGC/008/PRZ/MGA/APA/AGA/CPT | Milk Glass MGA | Velvet Black AGA | ATHLON PLUS Red | Cosmos Grey AGC | CPT - Plug type CNC |
| ABB/001/PRZ/PRZ/APA/ABB/DPT | Transparent Glass PRZ | White ABB | ATHLON PLUS Blue | White ABB | DPT - Plug type DNC |
| AGC/001/PRZ/PRZ/APA/ABB/DPT | Transparent Glass PRZ | White ABB | ATHLON PLUS Blue | Cosmos Grey AGC | DPT - Plug type DNC |
| ABB/002/PRZ/PRZ/APA/ABB/DPT | Transparent Glass PRZ | White ABB | ATHLON PLUS Dark grey | White ABB | DPT - Plug type DNC |
| AGC/002/PRZ/PRZ/APA/ABB/DPT | Transparent Glass PRZ | White ABB | ATHLON PLUS Dark grey | Cosmos Grey AGC | DPT - Plug type DNC |
| ABB/003/PRZ/PRZ/APA/ABB/DPT | Transparent Glass PRZ | White ABB | ATHLON PLUS Light grey | White ABB | DPT - Plug type DNC |
| AGC/003/PRZ/PRZ/APA/ABB/DPT | Transparent Glass PRZ | White ABB | ATHLON PLUS Light grey | Cosmos Grey AGC | DPT - Plug type DNC |
| ABB/004/PRZ/PRZ/APA/ABB/DPT | Transparent Glass PRZ | White ABB | ATHLON PLUS Light green | White ABB | DPT - Plug type DNC |
| AGC/004/PRZ/PRZ/APA/ABB/DPT | Transparent Glass PRZ | White ABB | ATHLON PLUS Light green | Cosmos Grey AGC | DPT - Plug type DNC |
| ABB/005/PRZ/PRZ/APA/ABB/DPT | Transparent Glass PRZ | White ABB | ATHLON PLUS Yellow | White ABB | DPT - Plug type DNC |
| AGC/005/PRZ/PRZ/APA/ABB/DPT | Transparent Glass PRZ | White ABB | ATHLON PLUS Yellow | Cosmos Grey AGC | DPT - Plug type DNC |
| ABB/006/PRZ/PRZ/APA/ABB/DPT | Transparent Glass PRZ | White ABB | ATHLON PLUS Orange | White ABB | DPT - Plug type DNC |
| AGC/006/PRZ/PRZ/APA/ABB/DPT | Transparent Glass PRZ | White ABB | ATHLON PLUS Orange | Cosmos Grey AGC | DPT - Plug type DNC |
| ABB/007/PRZ/PRZ/APA/ABB/DPT | Transparent Glass PRZ | White ABB | ATHLON PLUS Beige | White ABB | DPT - Plug type DNC |
| AGC/007/PRZ/PRZ/APA/ABB/DPT | Transparent Glass PRZ | White ABB | ATHLON PLUS Beige | Cosmos Grey AGC | DPT - Plug type DNC |
| ABB/008/PRZ/PRZ/APA/ABB/DPT | Transparent Glass PRZ | White ABB | ATHLON PLUS Red | White ABB | DPT - Plug type DNC |
| AGC/008/PRZ/PRZ/APA/ABB/DPT | Transparent Glass PRZ | White ABB | ATHLON PLUS Red | Cosmos Grey AGC | DPT - Plug type DNC |
| ABB/001/PRZ/MGA/APA/ABB/DPT | Milk Glass MGA | White ABB | ATHLON PLUS Blue | White ABB | DPT - Plug type DNC |
| AGC/001/PRZ/MGA/APA/ABB/DPT | Milk Glass MGA | White ABB | ATHLON PLUS Blue | Cosmos Grey AGC | DPT - Plug type DNC |
| ABB/002/PRZ/MGA/APA/ABB/DPT | Milk Glass MGA | White ABB | ATHLON PLUS Dark grey | White ABB | DPT - Plug type DNC |
| AGC/002/PRZ/MGA/APA/ABB/DPT | Milk Glass MGA | White ABB | ATHLON PLUS Dark grey | Cosmos Grey AGC | DPT - Plug type DNC |
| ABB/003/PRZ/MGA/APA/ABB/DPT | Milk Glass MGA | White ABB | ATHLON PLUS Light grey | White ABB | DPT - Plug type DNC |
| AGC/003/PRZ/MGA/APA/ABB/DPT | Milk Glass MGA | White ABB | ATHLON PLUS Light grey | Cosmos Grey AGC | DPT - Plug type DNC |
| ABB/004/PRZ/MGA/APA/ABB/DPT | Milk Glass MGA | White ABB | ATHLON PLUS Light green | White ABB | DPT - Plug type DNC |
| AGC/004/PRZ/MGA/APA/ABB/DPT | Milk Glass MGA | White ABB | ATHLON PLUS Light green | Cosmos Grey AGC | DPT - Plug type DNC |
| ABB/005/PRZ/MGA/APA/ABB/DPT | Milk Glass MGA | White ABB | ATHLON PLUS Yellow | White ABB | DPT - Plug type DNC |
| AGC/005/PRZ/MGA/APA/ABB/DPT | Milk Glass MGA | White ABB | ATHLON PLUS Yellow | Cosmos Grey AGC | DPT - Plug type DNC |
| ABB/006/PRZ/MGA/APA/ABB/DPT | Milk Glass MGA | White ABB | ATHLON PLUS Orange | White ABB | DPT - Plug type DNC |
| AGC/006/PRZ/MGA/APA/ABB/DPT | Milk Glass MGA | White ABB | ATHLON PLUS Orange | Cosmos Grey AGC | DPT - Plug type DNC |
| ABB/007/PRZ/MGA/APA/ABB/DPT | Milk Glass MGA | White ABB | ATHLON PLUS Beige | White ABB | DPT - Plug type DNC |
| AGC/007/PRZ/MGA/APA/ABB/DPT | Milk Glass MGA | White ABB | ATHLON PLUS Beige | Cosmos Grey AGC | DPT - Plug type DNC |
| ABB/008/PRZ/MGA/APA/ABB/DPT | Milk Glass MGA | White ABB | ATHLON PLUS Red | White ABB | DPT - Plug type DNC |
| AGC/008/PRZ/MGA/APA/ABB/DPT | Milk Glass MGA | White ABB | ATHLON PLUS Red | Cosmos Grey AGC | DPT - Plug type DNC |
| ABB/001/PRZ/PRZ/APA/AGA/DPT | Transparent Glass PRZ | Velvet Black AGA | ATHLON PLUS Blue | White ABB | DPT - Plug type DNC |
| AGC/001/PRZ/PRZ/APA/AGA/DPT | Transparent Glass PRZ | Velvet Black AGA | ATHLON PLUS Blue | Cosmos Grey AGC | DPT - Plug type DNC |
| ABB/002/PRZ/PRZ/APA/AGA/DPT | Transparent Glass PRZ | Velvet Black AGA | ATHLON PLUS Dark grey | White ABB | DPT - Plug type DNC |
| AGC/002/PRZ/PRZ/APA/AGA/DPT | Transparent Glass PRZ | Velvet Black AGA | ATHLON PLUS Dark grey | Cosmos Grey AGC | DPT - Plug type DNC |
| ABB/003/PRZ/PRZ/APA/AGA/DPT | Transparent Glass PRZ | Velvet Black AGA | ATHLON PLUS Light grey | White ABB | DPT - Plug type DNC |
| AGC/003/PRZ/PRZ/APA/AGA/DPT | Transparent Glass PRZ | Velvet Black AGA | ATHLON PLUS Light grey | Cosmos Grey AGC | DPT - Plug type DNC |
| ABB/004/PRZ/PRZ/APA/AGA/DPT | Transparent Glass PRZ | Velvet Black AGA | ATHLON PLUS Light green | White ABB | DPT - Plug type DNC |
| AGC/004/PRZ/PRZ/APA/AGA/DPT | Transparent Glass PRZ | Velvet Black AGA | ATHLON PLUS Light green | Cosmos Grey AGC | DPT - Plug type DNC |
| ABB/005/PRZ/PRZ/APA/AGA/DPT | Transparent Glass PRZ | Velvet Black AGA | ATHLON PLUS Yellow | White ABB | DPT - Plug type DNC |
| AGC/005/PRZ/PRZ/APA/AGA/DPT | Transparent Glass PRZ | Velvet Black AGA | ATHLON PLUS Yellow | Cosmos Grey AGC | DPT - Plug type DNC |
| ABB/006/PRZ/PRZ/APA/AGA/DPT | Transparent Glass PRZ | Velvet Black AGA | ATHLON PLUS Orange | White ABB | DPT - Plug type DNC |
| AGC/006/PRZ/PRZ/APA/AGA/DPT | Transparent Glass PRZ | Velvet Black AGA | ATHLON PLUS Orange | Cosmos Grey AGC | DPT - Plug type DNC |
| ABB/007/PRZ/PRZ/APA/AGA/DPT | Transparent Glass PRZ | Velvet Black AGA | ATHLON PLUS Beige | White ABB | DPT - Plug type DNC |
| AGC/007/PRZ/PRZ/APA/AGA/DPT | Transparent Glass PRZ | Velvet Black AGA | ATHLON PLUS Beige | Cosmos Grey AGC | DPT - Plug type DNC |
| ABB/008/PRZ/PRZ/APA/AGA/DPT | Transparent Glass PRZ | Velvet Black AGA | ATHLON PLUS Red | White ABB | DPT - Plug type DNC |
| AGC/008/PRZ/PRZ/APA/AGA/DPT | Transparent Glass PRZ | Velvet Black AGA | ATHLON PLUS Red | Cosmos Grey AGC | DPT - Plug type DNC |
| ABB/001/PRZ/MGA/APA/AGA/DPT | Milk Glass MGA | Velvet Black AGA | ATHLON PLUS Blue | White ABB | DPT - Plug type DNC |
| AGC/001/PRZ/MGA/APA/AGA/DPT | Milk Glass MGA | Velvet Black AGA | ATHLON PLUS Blue | Cosmos Grey AGC | DPT - Plug type DNC |
| ABB/002/PRZ/MGA/APA/AGA/DPT | Milk Glass MGA | Velvet Black AGA | ATHLON PLUS Dark grey | White ABB | DPT - Plug type DNC |
| AGC/002/PRZ/MGA/APA/AGA/DPT | Milk Glass MGA | Velvet Black AGA | ATHLON PLUS Dark grey | Cosmos Grey AGC | DPT - Plug type DNC |
| ABB/003/PRZ/MGA/APA/AGA/DPT | Milk Glass MGA | Velvet Black AGA | ATHLON PLUS Light grey | White ABB | DPT - Plug type DNC |
| AGC/003/PRZ/MGA/APA/AGA/DPT | Milk Glass MGA | Velvet Black AGA | ATHLON PLUS Light grey | Cosmos Grey AGC | DPT - Plug type DNC |
| ABB/004/PRZ/MGA/APA/AGA/DPT | Milk Glass MGA | Velvet Black AGA | ATHLON PLUS Light green | White ABB | DPT - Plug type DNC |
| AGC/004/PRZ/MGA/APA/AGA/DPT | Milk Glass MGA | Velvet Black AGA | ATHLON PLUS Light green | Cosmos Grey AGC | DPT - Plug type DNC |
| ABB/005/PRZ/MGA/APA/AGA/DPT | Milk Glass MGA | Velvet Black AGA | ATHLON PLUS Yellow | White ABB | DPT - Plug type DNC |
| AGC/005/PRZ/MGA/APA/AGA/DPT | Milk Glass MGA | Velvet Black AGA | ATHLON PLUS Yellow | Cosmos Grey AGC | DPT - Plug type DNC |
| ABB/006/PRZ/MGA/APA/AGA/DPT | Milk Glass MGA | Velvet Black AGA | ATHLON PLUS Orange | White ABB | DPT - Plug type DNC |
| AGC/006/PRZ/MGA/APA/AGA/DPT | Milk Glass MGA | Velvet Black AGA | ATHLON PLUS Orange | Cosmos Grey AGC | DPT - Plug type DNC |
| ABB/007/PRZ/MGA/APA/AGA/DPT | Milk Glass MGA | Velvet Black AGA | ATHLON PLUS Beige | White ABB | DPT - Plug type DNC |
| AGC/007/PRZ/MGA/APA/AGA/DPT | Milk Glass MGA | Velvet Black AGA | ATHLON PLUS Beige | Cosmos Grey AGC | DPT - Plug type DNC |
| ABB/008/PRZ/MGA/APA/AGA/DPT | Milk Glass MGA | Velvet Black AGA | ATHLON PLUS Red | White ABB | DPT - Plug type DNC |
| AGC/008/PRZ/MGA/APA/AGA/DPT | Milk Glass MGA | Velvet Black AGA | ATHLON PLUS Red | Cosmos Grey AGC | DPT - Plug type DNC |

note: [stored X ft] marks values corroborated as IEEE doubles in the binary element streams (Revit-internal decimal feet)

## geometry (parser evidence)
native form markers: Blend x2, Sweep x66
no freeform markers — native parametric forms only
